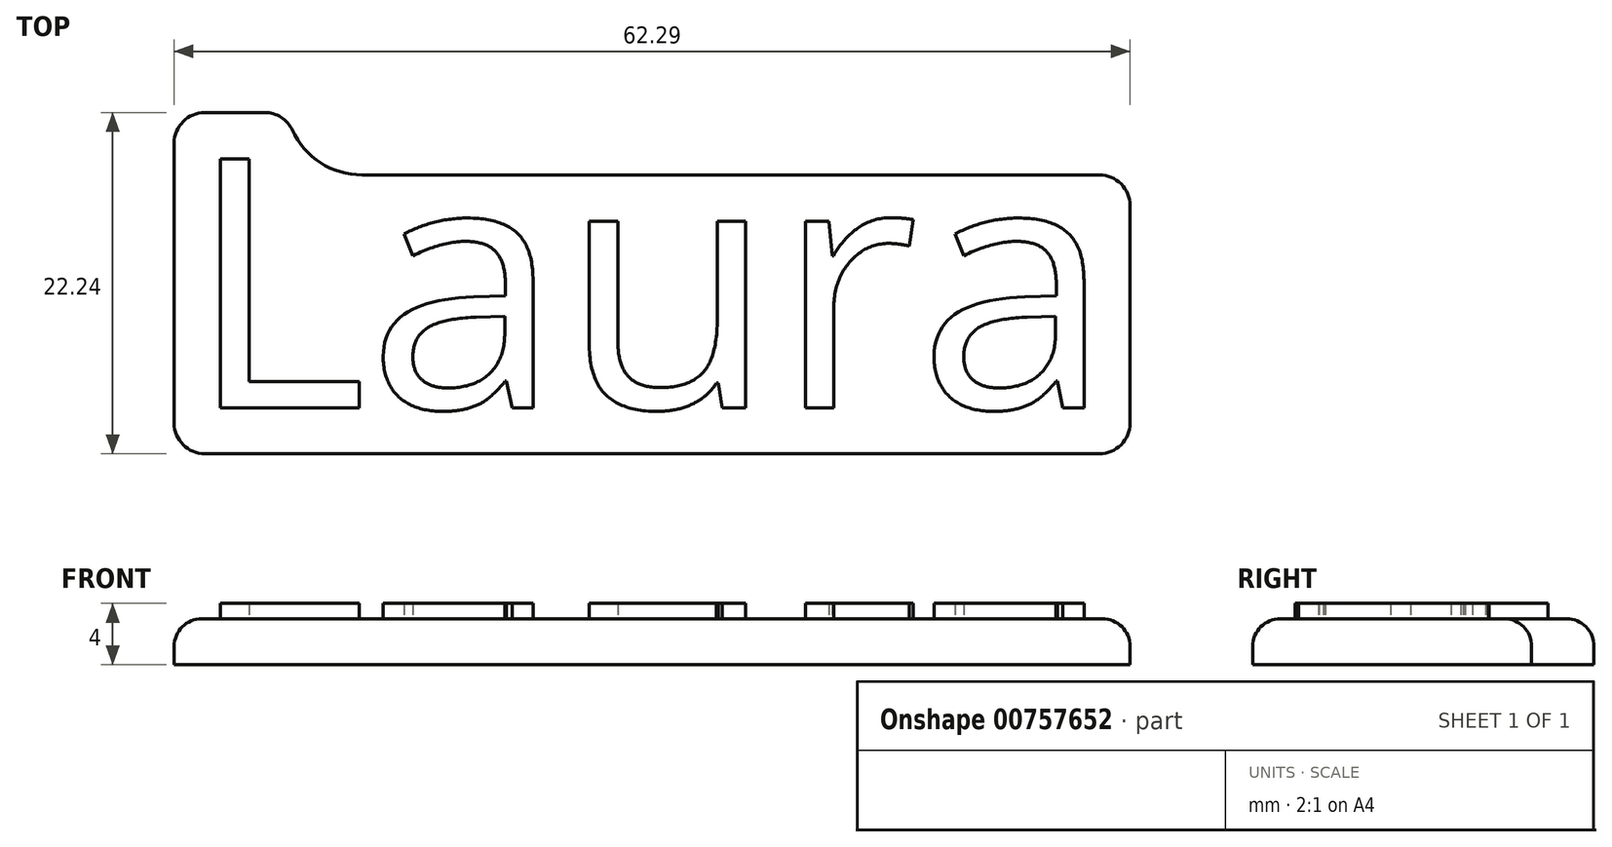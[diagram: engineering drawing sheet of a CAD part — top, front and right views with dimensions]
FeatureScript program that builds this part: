
annotation { "Feature Type Name" : "Feature", "Feature Type Description" : "" }
export const myFeature = defineFeature(function(context is Context, id is Id, definition is map)
    precondition{}
    {
        {
            var Q0;
            Q0=qCreatedBy(makeId("Top.planeOp"),FACE);
            var sketch = newSketch(context, id + "F0", { "sketchPlane" : qUnion([Q0])});
            skText(sketch, "E0", { "text": "Laura", "fontName": "OpenSans-Regular.ttf"});
            skLineSegment(sketch, "E1.bottom", {"start": v(-40, 18.2) * mm, "end": v(40, 18.2) * mm});
            skLineSegment(sketch, "E1.top", {"start": v(-40, -18.2) * mm, "end": v(40, -18.2) * mm});
            skLineSegment(sketch, "E1.left", {"start": v(-40, 18.2) * mm, "end": v(-40, -18.2) * mm});
            skLineSegment(sketch, "E1.right", {"start": v(40, 18.2) * mm, "end": v(40, -18.2) * mm});
            const initialGuessF0  = {"E0": [-0.03, -0.0082, 1, 0, 0.01638]};
            skSetInitialGuess(sketch, initialGuessF0);
            skSolve(sketch);
        }
        {
            var Q0;
            Q0=makeQuery(id+"F0.imprint","IMPRINT",FACE,{"disambiguationData":[TD([[makeQuery(id+"F0.imprint","IMPRINT",EDGE,{"derivedFrom":sQuery(id+"F0.wireOp",EDGE,"E0.sketch_text.stroke-6")}),-1.0]])]});
            var Q1;
            Q1=makeQuery(id+"F0.imprint","IMPRINT",FACE,{"disambiguationData":[TD([[makeQuery(id+"F0.imprint","IMPRINT",EDGE,{"derivedFrom":sQuery(id+"F0.wireOp",EDGE,"E0.sketch_text.stroke-0")}),-1.0]])]});
            var Q2;
            Q2=makeQuery(id+"F0.imprint","IMPRINT",FACE,{"disambiguationData":[TD([[makeQuery(id+"F0.imprint","IMPRINT",EDGE,{"derivedFrom":sQuery(id+"F0.wireOp",EDGE,"E0.sketch_text.stroke-33")}),-1.0]])]});
            var Q3;
            Q3=makeQuery(id+"F0.imprint","IMPRINT",FACE,{"disambiguationData":[TD([[makeQuery(id+"F0.imprint","IMPRINT",EDGE,{"derivedFrom":sQuery(id+"F0.wireOp",EDGE,"E0.sketch_text.stroke-50")}),-1.0]])]});
            var Q4;
            Q4=makeQuery(id+"F0.imprint","IMPRINT",FACE,{"disambiguationData":[TD([[makeQuery(id+"F0.imprint","IMPRINT",EDGE,{"derivedFrom":sQuery(id+"F0.wireOp",EDGE,"E0.sketch_text.stroke-63")}),-1.0]])]});
            extrude(context, id + "F1", {"entities" : qUnion([Q0, Q1, Q2, Q3, Q4]), "depth" : 4 * mm, "offsetDistance" : 25 * mm});
        }
        {
            var Q0;
            Q0=makeQuery(id+"F0.imprint","IMPRINT",FACE,{"disambiguationData":[TD([[makeQuery(id+"F0.imprint","IMPRINT",EDGE,{"derivedFrom":sQuery(id+"F0.wireOp",EDGE,"E0.sketch_text.stroke-0")}),1.0]])]});
            var Q1;
            Q1=makeQuery(id+"F0.imprint","IMPRINT",FACE,{"disambiguationData":[TD([[makeQuery(id+"F0.imprint","IMPRINT",EDGE,{"derivedFrom":sQuery(id+"F0.wireOp",EDGE,"E0.sketch_text.stroke-25")}),1.0]])]});
            var Q2;
            Q2=makeQuery(id+"F0.imprint","IMPRINT",FACE,{"disambiguationData":[TD([[makeQuery(id+"F0.imprint","IMPRINT",EDGE,{"derivedFrom":sQuery(id+"F0.wireOp",EDGE,"E0.sketch_text.stroke-82")}),1.0]])]});
            extrude(context, id + "F2", {"entities" : qUnion([Q0, Q1, Q2]), "operationType" : NewBodyOperationType.ADD, "depth" : 3 * mm, "offsetDistance" : 25 * mm});
        }
        {
            var Q0;
            {var subQ0=sQuery(id+"F0.wireOp",EDGE,"E0.sketch_text.stroke-89");var subQ1=sQuery(id+"F0.wireOp",EDGE,"E0.sketch_text.stroke-88");var subQ2=sQuery(id+"F0.wireOp",EDGE,"E0.sketch_text.stroke-87");var subQ3=sQuery(id+"F0.wireOp",EDGE,"E0.sketch_text.stroke-86");var subQ4=sQuery(id+"F0.wireOp",EDGE,"E0.sketch_text.stroke-85");var subQ5=sQuery(id+"F0.wireOp",EDGE,"E0.sketch_text.stroke-84");var subQ6=sQuery(id+"F0.wireOp",EDGE,"E0.sketch_text.stroke-83");var subQ7=sQuery(id+"F0.wireOp",EDGE,"E0.sketch_text.stroke-82");var subQ8=sQuery(id+"F0.wireOp",EDGE,"E0.sketch_text.stroke-32");var subQ9=sQuery(id+"F0.wireOp",EDGE,"E0.sketch_text.stroke-31");var subQ10=sQuery(id+"F0.wireOp",EDGE,"E0.sketch_text.stroke-30");var subQ11=sQuery(id+"F0.wireOp",EDGE,"E0.sketch_text.stroke-29");var subQ12=sQuery(id+"F0.wireOp",EDGE,"E0.sketch_text.stroke-28");var subQ13=sQuery(id+"F0.wireOp",EDGE,"E0.sketch_text.stroke-27");var subQ14=sQuery(id+"F0.wireOp",EDGE,"E0.sketch_text.stroke-26");var subQ15=sQuery(id+"F0.wireOp",EDGE,"E0.sketch_text.stroke-25");var subQ16=sQuery(id+"F0.wireOp",EDGE,"E0.sketch_text.stroke-81");var subQ17=sQuery(id+"F0.wireOp",EDGE,"E0.sketch_text.stroke-80");var subQ18=sQuery(id+"F0.wireOp",EDGE,"E0.sketch_text.stroke-79");var subQ19=sQuery(id+"F0.wireOp",EDGE,"E0.sketch_text.stroke-78");var subQ20=sQuery(id+"F0.wireOp",EDGE,"E0.sketch_text.stroke-77");var subQ21=sQuery(id+"F0.wireOp",EDGE,"E0.sketch_text.stroke-76");var subQ22=sQuery(id+"F0.wireOp",EDGE,"E0.sketch_text.stroke-75");var subQ23=sQuery(id+"F0.wireOp",EDGE,"E0.sketch_text.stroke-74");var subQ24=sQuery(id+"F0.wireOp",EDGE,"E0.sketch_text.stroke-73");var subQ25=sQuery(id+"F0.wireOp",EDGE,"E0.sketch_text.stroke-72");var subQ26=sQuery(id+"F0.wireOp",EDGE,"E0.sketch_text.stroke-71");var subQ27=sQuery(id+"F0.wireOp",EDGE,"E0.sketch_text.stroke-70");var subQ28=sQuery(id+"F0.wireOp",EDGE,"E0.sketch_text.stroke-69");var subQ29=sQuery(id+"F0.wireOp",EDGE,"E0.sketch_text.stroke-68");var subQ30=sQuery(id+"F0.wireOp",EDGE,"E0.sketch_text.stroke-67");var subQ31=sQuery(id+"F0.wireOp",EDGE,"E0.sketch_text.stroke-66");var subQ32=sQuery(id+"F0.wireOp",EDGE,"E0.sketch_text.stroke-65");var subQ33=sQuery(id+"F0.wireOp",EDGE,"E0.sketch_text.stroke-64");var subQ34=sQuery(id+"F0.wireOp",EDGE,"E0.sketch_text.stroke-63");var subQ35=sQuery(id+"F0.wireOp",EDGE,"E0.sketch_text.stroke-62");var subQ36=sQuery(id+"F0.wireOp",EDGE,"E0.sketch_text.stroke-61");var subQ37=sQuery(id+"F0.wireOp",EDGE,"E0.sketch_text.stroke-60");var subQ38=sQuery(id+"F0.wireOp",EDGE,"E0.sketch_text.stroke-59");var subQ39=sQuery(id+"F0.wireOp",EDGE,"E0.sketch_text.stroke-58");var subQ40=sQuery(id+"F0.wireOp",EDGE,"E0.sketch_text.stroke-57");var subQ41=sQuery(id+"F0.wireOp",EDGE,"E0.sketch_text.stroke-56");var subQ42=sQuery(id+"F0.wireOp",EDGE,"E0.sketch_text.stroke-55");var subQ43=sQuery(id+"F0.wireOp",EDGE,"E0.sketch_text.stroke-54");var subQ44=sQuery(id+"F0.wireOp",EDGE,"E0.sketch_text.stroke-53");var subQ45=sQuery(id+"F0.wireOp",EDGE,"E0.sketch_text.stroke-52");var subQ46=sQuery(id+"F0.wireOp",EDGE,"E0.sketch_text.stroke-51");var subQ47=sQuery(id+"F0.wireOp",EDGE,"E0.sketch_text.stroke-50");var subQ48=sQuery(id+"F0.wireOp",EDGE,"E0.sketch_text.stroke-49");var subQ49=sQuery(id+"F0.wireOp",EDGE,"E0.sketch_text.stroke-48");var subQ50=sQuery(id+"F0.wireOp",EDGE,"E0.sketch_text.stroke-47");var subQ51=sQuery(id+"F0.wireOp",EDGE,"E0.sketch_text.stroke-46");var subQ52=sQuery(id+"F0.wireOp",EDGE,"E0.sketch_text.stroke-45");var subQ53=sQuery(id+"F0.wireOp",EDGE,"E0.sketch_text.stroke-44");var subQ54=sQuery(id+"F0.wireOp",EDGE,"E0.sketch_text.stroke-43");var subQ55=sQuery(id+"F0.wireOp",EDGE,"E0.sketch_text.stroke-42");var subQ56=sQuery(id+"F0.wireOp",EDGE,"E0.sketch_text.stroke-41");var subQ57=sQuery(id+"F0.wireOp",EDGE,"E0.sketch_text.stroke-40");var subQ58=sQuery(id+"F0.wireOp",EDGE,"E0.sketch_text.stroke-39");var subQ59=sQuery(id+"F0.wireOp",EDGE,"E0.sketch_text.stroke-38");var subQ60=sQuery(id+"F0.wireOp",EDGE,"E0.sketch_text.stroke-37");var subQ61=sQuery(id+"F0.wireOp",EDGE,"E0.sketch_text.stroke-36");var subQ62=sQuery(id+"F0.wireOp",EDGE,"E0.sketch_text.stroke-35");var subQ63=sQuery(id+"F0.wireOp",EDGE,"E0.sketch_text.stroke-34");var subQ64=sQuery(id+"F0.wireOp",EDGE,"E0.sketch_text.stroke-33");var subQ65=sQuery(id+"F0.wireOp",EDGE,"E0.sketch_text.stroke-24");var subQ66=sQuery(id+"F0.wireOp",EDGE,"E0.sketch_text.stroke-23");var subQ67=sQuery(id+"F0.wireOp",EDGE,"E0.sketch_text.stroke-22");var subQ68=sQuery(id+"F0.wireOp",EDGE,"E0.sketch_text.stroke-21");var subQ69=sQuery(id+"F0.wireOp",EDGE,"E0.sketch_text.stroke-20");var subQ70=sQuery(id+"F0.wireOp",EDGE,"E0.sketch_text.stroke-19");var subQ71=sQuery(id+"F0.wireOp",EDGE,"E0.sketch_text.stroke-18");var subQ72=sQuery(id+"F0.wireOp",EDGE,"E0.sketch_text.stroke-17");var subQ73=sQuery(id+"F0.wireOp",EDGE,"E0.sketch_text.stroke-16");var subQ74=sQuery(id+"F0.wireOp",EDGE,"E0.sketch_text.stroke-15");var subQ75=sQuery(id+"F0.wireOp",EDGE,"E0.sketch_text.stroke-14");var subQ76=sQuery(id+"F0.wireOp",EDGE,"E0.sketch_text.stroke-13");var subQ77=sQuery(id+"F0.wireOp",EDGE,"E0.sketch_text.stroke-12");var subQ78=sQuery(id+"F0.wireOp",EDGE,"E0.sketch_text.stroke-11");var subQ79=sQuery(id+"F0.wireOp",EDGE,"E0.sketch_text.stroke-10");var subQ80=sQuery(id+"F0.wireOp",EDGE,"E0.sketch_text.stroke-9");var subQ81=sQuery(id+"F0.wireOp",EDGE,"E0.sketch_text.stroke-8");var subQ82=sQuery(id+"F0.wireOp",EDGE,"E0.sketch_text.stroke-7");var subQ83=sQuery(id+"F0.wireOp",EDGE,"E0.sketch_text.stroke-6");var subQ84=sQuery(id+"F0.wireOp",EDGE,"E0.sketch_text.stroke-5");var subQ85=sQuery(id+"F0.wireOp",EDGE,"E0.sketch_text.stroke-4");var subQ86=sQuery(id+"F0.wireOp",EDGE,"E0.sketch_text.stroke-3");var subQ87=sQuery(id+"F0.wireOp",EDGE,"E0.sketch_text.stroke-2");var subQ88=sQuery(id+"F0.wireOp",EDGE,"E0.sketch_text.stroke-1");var subQ89=sQuery(id+"F0.wireOp",EDGE,"E0.sketch_text.stroke-0");Q0=makeQuery(id+"F2.boolean.opBoolean","MERGE",FACE,{"derivedFrom":[makeQuery(id+"F1.opExtrude","CAP_FACE",FACE,{"disambiguationData":[OSD([subQ89,subQ88,subQ87,subQ86,subQ85,subQ84])],"isStart":true}),makeQuery(id+"F1.opExtrude","CAP_FACE",FACE,{"disambiguationData":[OSD([subQ83,subQ82,subQ81,subQ80,subQ79,subQ78,subQ77,subQ76,subQ75,subQ74,subQ73,subQ72,subQ71,subQ70,subQ69,subQ68,subQ67,subQ66,subQ65,subQ15,subQ14,subQ13,subQ12,subQ11,subQ10,subQ9,subQ8])],"isStart":true}),makeQuery(id+"F1.opExtrude","CAP_FACE",FACE,{"disambiguationData":[OSD([subQ64,subQ63,subQ62,subQ61,subQ60,subQ59,subQ58,subQ57,subQ56,subQ55,subQ54,subQ53,subQ52,subQ51,subQ50,subQ49,subQ48])],"isStart":true}),makeQuery(id+"F1.opExtrude","CAP_FACE",FACE,{"disambiguationData":[OSD([subQ47,subQ46,subQ45,subQ44,subQ43,subQ42,subQ41,subQ40,subQ39,subQ38,subQ37,subQ36,subQ35])],"isStart":true}),makeQuery(id+"F1.opExtrude","CAP_FACE",FACE,{"disambiguationData":[OSD([subQ34,subQ33,subQ32,subQ31,subQ30,subQ29,subQ28,subQ27,subQ26,subQ25,subQ24,subQ23,subQ22,subQ21,subQ20,subQ19,subQ18,subQ17,subQ16,subQ7,subQ6,subQ5,subQ4,subQ3,subQ2,subQ1,subQ0])],"isStart":true}),makeQuery(id+"F2.opExtrude","CAP_FACE",FACE,{"disambiguationData":[OSD([subQ89,subQ88,subQ87,subQ86,subQ85,subQ84,subQ83,subQ82,subQ81,subQ80,subQ79,subQ78,subQ77,subQ76,subQ75,subQ74,subQ73,subQ72,subQ71,subQ70,subQ69,subQ68,subQ67,subQ66,subQ65,subQ64,subQ63,subQ62,subQ61,subQ60,subQ59,subQ58,subQ57,subQ56,subQ55,subQ54,subQ53,subQ52,subQ51,subQ50,subQ49,subQ48,subQ47,subQ46,subQ45,subQ44,subQ43,subQ42,subQ41,subQ40,subQ39,subQ38,subQ37,subQ36,subQ35,subQ34,subQ33,subQ32,subQ31,subQ30,subQ29,subQ28,subQ27,subQ26,subQ25,subQ24,subQ23,subQ22,subQ21,subQ20,subQ19,subQ18,subQ17,subQ16,sQuery(id+"F0.wireOp",EDGE,"E1.bottom"),sQuery(id+"F0.wireOp",EDGE,"E1.top"),sQuery(id+"F0.wireOp",EDGE,"E1.left"),sQuery(id+"F0.wireOp",EDGE,"E1.right")])],"isStart":true}),makeQuery(id+"F2.opExtrude","CAP_FACE",FACE,{"disambiguationData":[OSD([subQ15,subQ14,subQ13,subQ12,subQ11,subQ10,subQ9,subQ8])],"isStart":true}),makeQuery(id+"F2.opExtrude","CAP_FACE",FACE,{"disambiguationData":[OSD([subQ7,subQ6,subQ5,subQ4,subQ3,subQ2,subQ1,subQ0])],"isStart":true})]});}
            var sketch = newSketch(context, id + "F3", { "sketchPlane" : qUnion([Q0])});
            skLineSegment(sketch, "E2.0.0", {"start": v(-40, -18.2) * mm, "end": v(-40, 18.2) * mm});
            skLineSegment(sketch, "E2.0.1", {"start": v(-40, 18.2) * mm, "end": v(40, 18.2) * mm});
            skLineSegment(sketch, "E2.0.2", {"start": v(40, 18.2) * mm, "end": v(40, -18.2) * mm});
            skLineSegment(sketch, "E2.0.3", {"start": v(40, -18.2) * mm, "end": v(-40, -18.2) * mm});
            skLineSegment(sketch, "E3.0.0", {"start": v(-27.77, 8.2) * mm, "end": v(-18.71, 8.2) * mm});
            skLineSegment(sketch, "E3.0.1", {"start": v(-18.71, 8.2) * mm, "end": v(-18.71, 6.48) * mm});
            skLineSegment(sketch, "E3.0.2", {"start": v(-18.71, 6.48) * mm, "end": v(-25.88, 6.48) * mm});
            skLineSegment(sketch, "E3.0.3", {"start": v(-25.88, 6.48) * mm, "end": v(-25.88, -8.05) * mm});
            skLineSegment(sketch, "E3.0.4", {"start": v(-25.88, -8.05) * mm, "end": v(-27.77, -8.05) * mm});
            skLineSegment(sketch, "E3.0.5", {"start": v(-27.77, -8.05) * mm, "end": v(-27.77, 8.2) * mm});
            skLineSegment(sketch, "E3.1.0", {"start": v(-8.75, 8.2) * mm, "end": v(-7.38, 8.2) * mm});
            skLineSegment(sketch, "E3.1.1", {"start": v(-7.38, 8.2) * mm, "end": v(-7.38, -0.12) * mm});
            skFitSpline(sketch, "E3.1.2", {"points": [v(-3.7, -0.06) * mm, v(-3.7, -1.13) * mm, v(-4.22, -1.6) * mm]});
            skFitSpline(sketch, "E3.1.3", {"points": [v(-4.22, -1.6) * mm, v(-4.74, -2.1) * mm, v(-5.83, -2.1) * mm]});
            skFitSpline(sketch, "E3.1.4", {"points": [v(-5.83, -2.1) * mm, v(-6.37, -2.1) * mm, v(-6.9, -1.95) * mm]});
            skFitSpline(sketch, "E3.1.5", {"points": [v(-6.9, -1.95) * mm, v(-7.44, -1.81) * mm, v(-7.9, -1.57) * mm]});
            skLineSegment(sketch, "E3.1.6", {"start": v(-15.78, -3.14) * mm, "end": v(-15.21, -1.73) * mm});
            skFitSpline(sketch, "E3.1.7", {"points": [v(-7.6, -0.87) * mm, v(-6.65, -1.33) * mm, v(-5.89, -1.33) * mm]});
            skFitSpline(sketch, "E3.1.8", {"points": [v(-5.89, -1.33) * mm, v(-5.2, -1.33) * mm, v(-4.9, -1) * mm]});
            skFitSpline(sketch, "E3.1.9", {"points": [v(-4.9, -1) * mm, v(-4.6, -0.65) * mm, v(-4.6, 0.07) * mm]});
            skLineSegment(sketch, "E3.1.10", {"start": v(-9.18, 0.14) * mm, "end": v(-9.18, 0.9) * mm});
            skLineSegment(sketch, "E3.1.11", {"start": v(-9.18, 0.9) * mm, "end": v(-11.25, 0.96) * mm});
            skFitSpline(sketch, "E3.1.12", {"points": [v(-5.62, 0.48) * mm, v(-8.57, 0.57) * mm, v(-8.57, 2.41) * mm]});
            skFitSpline(sketch, "E3.1.13", {"points": [v(-8.57, 2.41) * mm, v(-8.57, 3.27) * mm, v(-8.06, 3.74) * mm]});
            skFitSpline(sketch, "E3.1.14", {"points": [v(-8.06, 3.74) * mm, v(-7.55, 4.2) * mm, v(-6.64, 4.2) * mm]});
            skFitSpline(sketch, "E3.1.15", {"points": [v(-6.64, 4.2) * mm, v(-5.96, 4.2) * mm, v(-5.5, 4) * mm]});
            skFitSpline(sketch, "E3.1.16", {"points": [v(-5.5, 4) * mm, v(-5.06, 3.8) * mm, v(-4.6, 3.23) * mm]});
            skLineSegment(sketch, "E3.1.17", {"start": v(-9.2, 6.46) * mm, "end": v(-9.11, 6.46) * mm});
            skLineSegment(sketch, "E3.1.18", {"start": v(-9.11, 6.46) * mm, "end": v(-8.75, 8.2) * mm});
            skLineSegment(sketch, "E3.2.0", {"start": v(-1.85, -3.99) * mm, "end": v(-3.71, -3.99) * mm});
            skLineSegment(sketch, "E3.2.1", {"start": v(-3.71, -3.99) * mm, "end": v(-3.71, 3.98) * mm});
            skFitSpline(sketch, "E3.2.2", {"points": [v(-1.86, 2) * mm, v(-1.86, 3.15) * mm, v(-1.3, 3.68) * mm]});
            skFitSpline(sketch, "E3.2.3", {"points": [v(-1.3, 3.68) * mm, v(-0.75, 4.2) * mm, v(0.36, 4.2) * mm]});
            skFitSpline(sketch, "E3.2.4", {"points": [v(0.36, 4.2) * mm, v(1, 4.2) * mm, v(1.5, 3.97) * mm]});
            skFitSpline(sketch, "E3.2.5", {"points": [v(1.5, 3.97) * mm, v(2, 3.73) * mm, v(2.3, 3.28) * mm]});
            skLineSegment(sketch, "E3.2.6", {"start": v(4.58, 6.56) * mm, "end": v(4.68, 6.56) * mm});
            skLineSegment(sketch, "E3.2.7", {"start": v(4.68, 6.56) * mm, "end": v(4.95, 8.2) * mm});
            skLineSegment(sketch, "E3.2.8", {"start": v(4.95, 8.2) * mm, "end": v(6.47, 8.2) * mm});
            skLineSegment(sketch, "E3.2.9", {"start": v(6.47, 8.2) * mm, "end": v(6.47, -3.99) * mm});
            skLineSegment(sketch, "E3.2.10", {"start": v(6.47, -3.99) * mm, "end": v(4.62, -3.99) * mm});
            skLineSegment(sketch, "E3.2.11", {"start": v(4.62, -3.99) * mm, "end": v(4.62, 2.41) * mm});
            skFitSpline(sketch, "E3.2.12", {"points": [v(2.31, 1.2) * mm, v(2.31, 2.4) * mm, v(1.87, 2.91) * mm]});
            skFitSpline(sketch, "E3.2.13", {"points": [v(1.87, 2.91) * mm, v(1.43, 3.43) * mm, v(0.47, 3.43) * mm]});
            skFitSpline(sketch, "E3.2.14", {"points": [v(0.47, 3.43) * mm, v(-0.25, 3.43) * mm, v(-0.59, 3.07) * mm]});
            skFitSpline(sketch, "E3.2.15", {"points": [v(-0.59, 3.07) * mm, v(-0.92, 2.7) * mm, v(-0.92, 1.96) * mm]});
            skLineSegment(sketch, "E3.2.16", {"start": v(-1.85, 3.91) * mm, "end": v(-1.85, -3.99) * mm});
            skFitSpline(sketch, "E3.3.0", {"points": [v(7.97, -2.1) * mm, v(7.4, -2.1) * mm, v(6.92, -1.78) * mm]});
            skFitSpline(sketch, "E3.3.1", {"points": [v(6.92, -1.78) * mm, v(6.44, -1.46) * mm, v(6.1, -0.87) * mm]});
            skLineSegment(sketch, "E3.3.2", {"start": v(12.2, -1.73) * mm, "end": v(12.12, -1.73) * mm});
            skLineSegment(sketch, "E3.3.3", {"start": v(12.12, -1.73) * mm, "end": v(11.9, -3.99) * mm});
            skLineSegment(sketch, "E3.3.4", {"start": v(11.9, -3.99) * mm, "end": v(10.38, -3.99) * mm});
            skLineSegment(sketch, "E3.3.5", {"start": v(10.38, -3.99) * mm, "end": v(10.38, 8.2) * mm});
            skLineSegment(sketch, "E3.3.6", {"start": v(10.38, 8.2) * mm, "end": v(12.23, 8.2) * mm});
            skLineSegment(sketch, "E3.3.7", {"start": v(12.23, 8.2) * mm, "end": v(12.23, 1.66) * mm});
            skFitSpline(sketch, "E3.3.8", {"points": [v(6.11, 0.83) * mm, v(6.11, -0.07) * mm, v(6.64, -0.67) * mm]});
            skFitSpline(sketch, "E3.3.9", {"points": [v(6.64, -0.67) * mm, v(7.16, -1.27) * mm, v(7.9, -1.27) * mm]});
            skFitSpline(sketch, "E3.3.10", {"points": [v(7.9, -1.27) * mm, v(8.2, -1.27) * mm, v(8.57, -1.18) * mm]});
            skLineSegment(sketch, "E3.3.11", {"start": v(17.13, -2.36) * mm, "end": v(17.4, -4.07) * mm});
            skFitSpline(sketch, "E3.3.12", {"points": [v(8.7, -2.04) * mm, v(8.37, -2.1) * mm, v(7.97, -2.1) * mm]});
            skLineSegment(sketch, "E3.4.0", {"start": v(27.16, 8.2) * mm, "end": v(28.52, 8.2) * mm});
            skLineSegment(sketch, "E3.4.1", {"start": v(28.52, 8.2) * mm, "end": v(28.52, -0.12) * mm});
            skFitSpline(sketch, "E3.4.2", {"points": [v(14.26, -0.06) * mm, v(14.26, -1.13) * mm, v(13.74, -1.6) * mm]});
            skFitSpline(sketch, "E3.4.3", {"points": [v(13.74, -1.6) * mm, v(13.21, -2.1) * mm, v(12.12, -2.1) * mm]});
            skFitSpline(sketch, "E3.4.4", {"points": [v(12.12, -2.1) * mm, v(11.58, -2.1) * mm, v(11.05, -1.95) * mm]});
            skFitSpline(sketch, "E3.4.5", {"points": [v(11.05, -1.95) * mm, v(10.51, -1.81) * mm, v(10.06, -1.57) * mm]});
            skLineSegment(sketch, "E3.4.6", {"start": v(20.12, -3.14) * mm, "end": v(20.7, -1.73) * mm});
            skFitSpline(sketch, "E3.4.7", {"points": [v(10.35, -0.87) * mm, v(11.3, -1.33) * mm, v(12.07, -1.33) * mm]});
            skFitSpline(sketch, "E3.4.8", {"points": [v(12.07, -1.33) * mm, v(12.75, -1.33) * mm, v(13.05, -1) * mm]});
            skFitSpline(sketch, "E3.4.9", {"points": [v(13.05, -1) * mm, v(13.36, -0.65) * mm, v(13.36, 0.07) * mm]});
            skLineSegment(sketch, "E3.4.10", {"start": v(26.72, 0.14) * mm, "end": v(26.72, 0.9) * mm});
            skLineSegment(sketch, "E3.4.11", {"start": v(26.72, 0.9) * mm, "end": v(24.66, 0.96) * mm});
            skFitSpline(sketch, "E3.4.12", {"points": [v(12.33, 0.48) * mm, v(9.38, 0.57) * mm, v(9.38, 2.41) * mm]});
            skFitSpline(sketch, "E3.4.13", {"points": [v(9.38, 2.41) * mm, v(9.38, 3.27) * mm, v(9.9, 3.74) * mm]});
            skFitSpline(sketch, "E3.4.14", {"points": [v(9.9, 3.74) * mm, v(10.4, 4.2) * mm, v(11.31, 4.2) * mm]});
            skFitSpline(sketch, "E3.4.15", {"points": [v(11.31, 4.2) * mm, v(12, 4.2) * mm, v(12.44, 4) * mm]});
            skFitSpline(sketch, "E3.4.16", {"points": [v(12.44, 4) * mm, v(12.9, 3.8) * mm, v(13.35, 3.23) * mm]});
            skLineSegment(sketch, "E3.4.17", {"start": v(26.7, 6.46) * mm, "end": v(26.79, 6.46) * mm});
            skLineSegment(sketch, "E3.4.18", {"start": v(26.79, 6.46) * mm, "end": v(27.16, 8.2) * mm});
            skFitSpline(sketch, "E4.0.0", {"points": [v(-7.6, 2.42) * mm, v(-7.6, 2.92) * mm, v(-7.3, 3.18) * mm]});
            skFitSpline(sketch, "E4.0.1", {"points": [v(-7.3, 3.18) * mm, v(-7, 3.44) * mm, v(-6.46, 3.44) * mm]});
            skFitSpline(sketch, "E4.0.2", {"points": [v(-6.46, 3.44) * mm, v(-5.6, 3.44) * mm, v(-5.1, 2.97) * mm]});
            skFitSpline(sketch, "E4.0.3", {"points": [v(-5.1, 2.97) * mm, v(-4.61, 2.5) * mm, v(-4.61, 1.65) * mm]});
            skLineSegment(sketch, "E4.0.4", {"start": v(-9.23, 3.3) * mm, "end": v(-9.23, 2.2) * mm});
            skLineSegment(sketch, "E4.0.5", {"start": v(-9.23, 2.2) * mm, "end": v(-11.07, 2.28) * mm});
            skFitSpline(sketch, "E4.0.6", {"points": [v(-5.54, 1.14) * mm, v(-6.64, 1.18) * mm, v(-7.12, 1.48) * mm]});
            skFitSpline(sketch, "E4.0.7", {"points": [v(-7.12, 1.48) * mm, v(-7.6, 1.78) * mm, v(-7.6, 2.42) * mm]});
            skFitSpline(sketch, "E4.1.0", {"points": [v(10.35, 2.42) * mm, v(10.35, 2.92) * mm, v(10.65, 3.18) * mm]});
            skFitSpline(sketch, "E4.1.1", {"points": [v(10.65, 3.18) * mm, v(10.95, 3.44) * mm, v(11.5, 3.44) * mm]});
            skFitSpline(sketch, "E4.1.2", {"points": [v(11.5, 3.44) * mm, v(12.36, 3.44) * mm, v(12.85, 2.97) * mm]});
            skFitSpline(sketch, "E4.1.3", {"points": [v(12.85, 2.97) * mm, v(13.34, 2.5) * mm, v(13.34, 1.65) * mm]});
            skLineSegment(sketch, "E4.1.4", {"start": v(26.68, 3.3) * mm, "end": v(26.68, 2.2) * mm});
            skLineSegment(sketch, "E4.1.5", {"start": v(26.68, 2.2) * mm, "end": v(24.83, 2.28) * mm});
            skFitSpline(sketch, "E4.1.6", {"points": [v(12.42, 1.14) * mm, v(11.32, 1.18) * mm, v(10.83, 1.48) * mm]});
            skFitSpline(sketch, "E4.1.7", {"points": [v(10.83, 1.48) * mm, v(10.35, 1.78) * mm, v(10.35, 2.42) * mm]});
            skLineSegment(sketch, "E5.0", {"start": v(-30.77, 11.2) * mm, "end": v(31.52, 11.2) * mm});
            skLineSegment(sketch, "E5.1", {"start": v(-30.77, -11.05) * mm, "end": v(-30.77, 11.2) * mm});
            skLineSegment(sketch, "E5.2", {"start": v(-22.88, -11.05) * mm, "end": v(-30.77, -11.05) * mm});
            skLineSegment(sketch, "E6", {"start": v(31.52, -6.99) * mm, "end": v(31.52, 11.2) * mm});
            skLineSegment(sketch, "E7", {"start": v(31.52, -6.99) * mm, "end": v(-22.88, -6.99) * mm});
            skLineSegment(sketch, "E8", {"start": v(-22.88, -6.99) * mm, "end": v(-22.88, -11.05) * mm});
            skSolve(sketch);
        }
        {
            var Q0;
            Q0=makeQuery(id+"F3.imprint","IMPRINT",FACE,{"disambiguationData":[TD([[makeQuery(id+"F3.imprint","IMPRINT",EDGE,{"derivedFrom":sQuery(id+"F3.wireOp",EDGE,"E2.0.0")}),-1.0]])]});
            extrude(context, id + "F4", {"entities" : qUnion([Q0]), "operationType" : NewBodyOperationType.REMOVE, "oppositeDirection" : true, "depth" : 25 * mm, "offsetDistance" : 25 * mm});
        }
        {
            var Q0;
            Q0=makeQuery(id+"F4.boolean.opBoolean","COPY",EDGE,{"derivedFrom":makeQuery(id+"F4.opExtrude","SWEPT_EDGE",EDGE,{"disambiguationData":[OSD([sQuery(id+"F3.wireOp",EDGE,"E5.2"),sQuery(id+"F3.wireOp",EDGE,"E8")])]})});
            var Q1;
            Q1=makeQuery(id+"F4.boolean.opBoolean","COPY",EDGE,{"derivedFrom":makeQuery(id+"F4.opExtrude","SWEPT_EDGE",EDGE,{"disambiguationData":[OSD([sQuery(id+"F3.wireOp",EDGE,"E5.1"),sQuery(id+"F3.wireOp",EDGE,"E5.2")])]})});
            var Q2;
            Q2=makeQuery(id+"F4.boolean.opBoolean","COPY",EDGE,{"derivedFrom":makeQuery(id+"F4.opExtrude","SWEPT_EDGE",EDGE,{"disambiguationData":[OSD([sQuery(id+"F3.wireOp",EDGE,"E5.0"),sQuery(id+"F3.wireOp",EDGE,"E5.1")])]})});
            var Q3;
            Q3=makeQuery(id+"F4.boolean.opBoolean","COPY",EDGE,{"derivedFrom":makeQuery(id+"F4.opExtrude","SWEPT_EDGE",EDGE,{"disambiguationData":[OSD([sQuery(id+"F3.wireOp",EDGE,"E5.0"),sQuery(id+"F3.wireOp",EDGE,"E6")])]})});
            var Q4;
            Q4=makeQuery(id+"F4.boolean.opBoolean","COPY",EDGE,{"derivedFrom":makeQuery(id+"F4.opExtrude","SWEPT_EDGE",EDGE,{"disambiguationData":[OSD([sQuery(id+"F3.wireOp",EDGE,"E6"),sQuery(id+"F3.wireOp",EDGE,"E7")])]})});
            fillet(context, id + "F5", {"entities" : qUnion([Q0, Q1, Q2, Q3, Q4]), "tangentPropagation" : true, "radius" : 2 * mm, "defaultsChanged" : true, "vertexSettings" : [], "allowEdgeOverflow" : false});
        }
        {
            var Q0;
            Q0=makeQuery(id+"F4.boolean.opBoolean","COPY",EDGE,{"derivedFrom":makeQuery(id+"F4.opExtrude","SWEPT_EDGE",EDGE,{"disambiguationData":[OSD([sQuery(id+"F3.wireOp",EDGE,"E7"),sQuery(id+"F3.wireOp",EDGE,"E8")])]})});
            fillet(context, id + "F6", {"entities" : qUnion([Q0]), "tangentPropagation" : true, "radius" : 5 * mm, "defaultsChanged" : false, "vertexSettings" : [], "allowEdgeOverflow" : false});
        }
        {
            var Q0;
            Q0=makeQuery(id+"F4.boolean.opBoolean","INTERSECT",EDGE,{"derivedFrom":[makeQuery(id+"F2.opExtrude","CAP_FACE",FACE,{"disambiguationData":[OSD([sQuery(id+"F0.wireOp",EDGE,"E0.sketch_text.stroke-0"),sQuery(id+"F0.wireOp",EDGE,"E0.sketch_text.stroke-1"),sQuery(id+"F0.wireOp",EDGE,"E0.sketch_text.stroke-2"),sQuery(id+"F0.wireOp",EDGE,"E0.sketch_text.stroke-3"),sQuery(id+"F0.wireOp",EDGE,"E0.sketch_text.stroke-4"),sQuery(id+"F0.wireOp",EDGE,"E0.sketch_text.stroke-5"),sQuery(id+"F0.wireOp",EDGE,"E0.sketch_text.stroke-6"),sQuery(id+"F0.wireOp",EDGE,"E0.sketch_text.stroke-7"),sQuery(id+"F0.wireOp",EDGE,"E0.sketch_text.stroke-8"),sQuery(id+"F0.wireOp",EDGE,"E0.sketch_text.stroke-9"),sQuery(id+"F0.wireOp",EDGE,"E0.sketch_text.stroke-10"),sQuery(id+"F0.wireOp",EDGE,"E0.sketch_text.stroke-11"),sQuery(id+"F0.wireOp",EDGE,"E0.sketch_text.stroke-12"),sQuery(id+"F0.wireOp",EDGE,"E0.sketch_text.stroke-13"),sQuery(id+"F0.wireOp",EDGE,"E0.sketch_text.stroke-14"),sQuery(id+"F0.wireOp",EDGE,"E0.sketch_text.stroke-15"),sQuery(id+"F0.wireOp",EDGE,"E0.sketch_text.stroke-16"),sQuery(id+"F0.wireOp",EDGE,"E0.sketch_text.stroke-17"),sQuery(id+"F0.wireOp",EDGE,"E0.sketch_text.stroke-18"),sQuery(id+"F0.wireOp",EDGE,"E0.sketch_text.stroke-19"),sQuery(id+"F0.wireOp",EDGE,"E0.sketch_text.stroke-20"),sQuery(id+"F0.wireOp",EDGE,"E0.sketch_text.stroke-21"),sQuery(id+"F0.wireOp",EDGE,"E0.sketch_text.stroke-22"),sQuery(id+"F0.wireOp",EDGE,"E0.sketch_text.stroke-23"),sQuery(id+"F0.wireOp",EDGE,"E0.sketch_text.stroke-24"),sQuery(id+"F0.wireOp",EDGE,"E0.sketch_text.stroke-33"),sQuery(id+"F0.wireOp",EDGE,"E0.sketch_text.stroke-34"),sQuery(id+"F0.wireOp",EDGE,"E0.sketch_text.stroke-35"),sQuery(id+"F0.wireOp",EDGE,"E0.sketch_text.stroke-36"),sQuery(id+"F0.wireOp",EDGE,"E0.sketch_text.stroke-37"),sQuery(id+"F0.wireOp",EDGE,"E0.sketch_text.stroke-38"),sQuery(id+"F0.wireOp",EDGE,"E0.sketch_text.stroke-39"),sQuery(id+"F0.wireOp",EDGE,"E0.sketch_text.stroke-40"),sQuery(id+"F0.wireOp",EDGE,"E0.sketch_text.stroke-41"),sQuery(id+"F0.wireOp",EDGE,"E0.sketch_text.stroke-42"),sQuery(id+"F0.wireOp",EDGE,"E0.sketch_text.stroke-43"),sQuery(id+"F0.wireOp",EDGE,"E0.sketch_text.stroke-44"),sQuery(id+"F0.wireOp",EDGE,"E0.sketch_text.stroke-45"),sQuery(id+"F0.wireOp",EDGE,"E0.sketch_text.stroke-46"),sQuery(id+"F0.wireOp",EDGE,"E0.sketch_text.stroke-47"),sQuery(id+"F0.wireOp",EDGE,"E0.sketch_text.stroke-48"),sQuery(id+"F0.wireOp",EDGE,"E0.sketch_text.stroke-49"),sQuery(id+"F0.wireOp",EDGE,"E0.sketch_text.stroke-50"),sQuery(id+"F0.wireOp",EDGE,"E0.sketch_text.stroke-51"),sQuery(id+"F0.wireOp",EDGE,"E0.sketch_text.stroke-52"),sQuery(id+"F0.wireOp",EDGE,"E0.sketch_text.stroke-53"),sQuery(id+"F0.wireOp",EDGE,"E0.sketch_text.stroke-54"),sQuery(id+"F0.wireOp",EDGE,"E0.sketch_text.stroke-55"),sQuery(id+"F0.wireOp",EDGE,"E0.sketch_text.stroke-56"),sQuery(id+"F0.wireOp",EDGE,"E0.sketch_text.stroke-57"),sQuery(id+"F0.wireOp",EDGE,"E0.sketch_text.stroke-58"),sQuery(id+"F0.wireOp",EDGE,"E0.sketch_text.stroke-59"),sQuery(id+"F0.wireOp",EDGE,"E0.sketch_text.stroke-60"),sQuery(id+"F0.wireOp",EDGE,"E0.sketch_text.stroke-61"),sQuery(id+"F0.wireOp",EDGE,"E0.sketch_text.stroke-62"),sQuery(id+"F0.wireOp",EDGE,"E0.sketch_text.stroke-63"),sQuery(id+"F0.wireOp",EDGE,"E0.sketch_text.stroke-64"),sQuery(id+"F0.wireOp",EDGE,"E0.sketch_text.stroke-65"),sQuery(id+"F0.wireOp",EDGE,"E0.sketch_text.stroke-66"),sQuery(id+"F0.wireOp",EDGE,"E0.sketch_text.stroke-67"),sQuery(id+"F0.wireOp",EDGE,"E0.sketch_text.stroke-68"),sQuery(id+"F0.wireOp",EDGE,"E0.sketch_text.stroke-69"),sQuery(id+"F0.wireOp",EDGE,"E0.sketch_text.stroke-70"),sQuery(id+"F0.wireOp",EDGE,"E0.sketch_text.stroke-71"),sQuery(id+"F0.wireOp",EDGE,"E0.sketch_text.stroke-72"),sQuery(id+"F0.wireOp",EDGE,"E0.sketch_text.stroke-73"),sQuery(id+"F0.wireOp",EDGE,"E0.sketch_text.stroke-74"),sQuery(id+"F0.wireOp",EDGE,"E0.sketch_text.stroke-75"),sQuery(id+"F0.wireOp",EDGE,"E0.sketch_text.stroke-76"),sQuery(id+"F0.wireOp",EDGE,"E0.sketch_text.stroke-77"),sQuery(id+"F0.wireOp",EDGE,"E0.sketch_text.stroke-78"),sQuery(id+"F0.wireOp",EDGE,"E0.sketch_text.stroke-79"),sQuery(id+"F0.wireOp",EDGE,"E0.sketch_text.stroke-80"),sQuery(id+"F0.wireOp",EDGE,"E0.sketch_text.stroke-81"),sQuery(id+"F0.wireOp",EDGE,"E1.bottom"),sQuery(id+"F0.wireOp",EDGE,"E1.top"),sQuery(id+"F0.wireOp",EDGE,"E1.left"),sQuery(id+"F0.wireOp",EDGE,"E1.right")])],"isStart":false}),makeQuery(id+"F4.opExtrude","SWEPT_FACE",FACE,{"disambiguationData":[OSD([sQuery(id+"F3.wireOp",EDGE,"E5.0")])]})]});
            var Q1;
            Q1=makeQuery(id+"F5.opFillet","BLEND_EDGE",EDGE,{"blendedFrom":[makeQuery(id+"F4.boolean.opBoolean","COPY",EDGE,{"derivedFrom":makeQuery(id+"F4.opExtrude","SWEPT_EDGE",EDGE,{"disambiguationData":[OSD([sQuery(id+"F3.wireOp",EDGE,"E5.0"),sQuery(id+"F3.wireOp",EDGE,"E5.1")])]})}),makeQuery(id+"F2.opExtrude","CAP_FACE",FACE,{"disambiguationData":[OSD([sQuery(id+"F0.wireOp",EDGE,"E0.sketch_text.stroke-0"),sQuery(id+"F0.wireOp",EDGE,"E0.sketch_text.stroke-1"),sQuery(id+"F0.wireOp",EDGE,"E0.sketch_text.stroke-2"),sQuery(id+"F0.wireOp",EDGE,"E0.sketch_text.stroke-3"),sQuery(id+"F0.wireOp",EDGE,"E0.sketch_text.stroke-4"),sQuery(id+"F0.wireOp",EDGE,"E0.sketch_text.stroke-5"),sQuery(id+"F0.wireOp",EDGE,"E0.sketch_text.stroke-6"),sQuery(id+"F0.wireOp",EDGE,"E0.sketch_text.stroke-7"),sQuery(id+"F0.wireOp",EDGE,"E0.sketch_text.stroke-8"),sQuery(id+"F0.wireOp",EDGE,"E0.sketch_text.stroke-9"),sQuery(id+"F0.wireOp",EDGE,"E0.sketch_text.stroke-10"),sQuery(id+"F0.wireOp",EDGE,"E0.sketch_text.stroke-11"),sQuery(id+"F0.wireOp",EDGE,"E0.sketch_text.stroke-12"),sQuery(id+"F0.wireOp",EDGE,"E0.sketch_text.stroke-13"),sQuery(id+"F0.wireOp",EDGE,"E0.sketch_text.stroke-14"),sQuery(id+"F0.wireOp",EDGE,"E0.sketch_text.stroke-15"),sQuery(id+"F0.wireOp",EDGE,"E0.sketch_text.stroke-16"),sQuery(id+"F0.wireOp",EDGE,"E0.sketch_text.stroke-17"),sQuery(id+"F0.wireOp",EDGE,"E0.sketch_text.stroke-18"),sQuery(id+"F0.wireOp",EDGE,"E0.sketch_text.stroke-19"),sQuery(id+"F0.wireOp",EDGE,"E0.sketch_text.stroke-20"),sQuery(id+"F0.wireOp",EDGE,"E0.sketch_text.stroke-21"),sQuery(id+"F0.wireOp",EDGE,"E0.sketch_text.stroke-22"),sQuery(id+"F0.wireOp",EDGE,"E0.sketch_text.stroke-23"),sQuery(id+"F0.wireOp",EDGE,"E0.sketch_text.stroke-24"),sQuery(id+"F0.wireOp",EDGE,"E0.sketch_text.stroke-33"),sQuery(id+"F0.wireOp",EDGE,"E0.sketch_text.stroke-34"),sQuery(id+"F0.wireOp",EDGE,"E0.sketch_text.stroke-35"),sQuery(id+"F0.wireOp",EDGE,"E0.sketch_text.stroke-36"),sQuery(id+"F0.wireOp",EDGE,"E0.sketch_text.stroke-37"),sQuery(id+"F0.wireOp",EDGE,"E0.sketch_text.stroke-38"),sQuery(id+"F0.wireOp",EDGE,"E0.sketch_text.stroke-39"),sQuery(id+"F0.wireOp",EDGE,"E0.sketch_text.stroke-40"),sQuery(id+"F0.wireOp",EDGE,"E0.sketch_text.stroke-41"),sQuery(id+"F0.wireOp",EDGE,"E0.sketch_text.stroke-42"),sQuery(id+"F0.wireOp",EDGE,"E0.sketch_text.stroke-43"),sQuery(id+"F0.wireOp",EDGE,"E0.sketch_text.stroke-44"),sQuery(id+"F0.wireOp",EDGE,"E0.sketch_text.stroke-45"),sQuery(id+"F0.wireOp",EDGE,"E0.sketch_text.stroke-46"),sQuery(id+"F0.wireOp",EDGE,"E0.sketch_text.stroke-47"),sQuery(id+"F0.wireOp",EDGE,"E0.sketch_text.stroke-48"),sQuery(id+"F0.wireOp",EDGE,"E0.sketch_text.stroke-49"),sQuery(id+"F0.wireOp",EDGE,"E0.sketch_text.stroke-50"),sQuery(id+"F0.wireOp",EDGE,"E0.sketch_text.stroke-51"),sQuery(id+"F0.wireOp",EDGE,"E0.sketch_text.stroke-52"),sQuery(id+"F0.wireOp",EDGE,"E0.sketch_text.stroke-53"),sQuery(id+"F0.wireOp",EDGE,"E0.sketch_text.stroke-54"),sQuery(id+"F0.wireOp",EDGE,"E0.sketch_text.stroke-55"),sQuery(id+"F0.wireOp",EDGE,"E0.sketch_text.stroke-56"),sQuery(id+"F0.wireOp",EDGE,"E0.sketch_text.stroke-57"),sQuery(id+"F0.wireOp",EDGE,"E0.sketch_text.stroke-58"),sQuery(id+"F0.wireOp",EDGE,"E0.sketch_text.stroke-59"),sQuery(id+"F0.wireOp",EDGE,"E0.sketch_text.stroke-60"),sQuery(id+"F0.wireOp",EDGE,"E0.sketch_text.stroke-61"),sQuery(id+"F0.wireOp",EDGE,"E0.sketch_text.stroke-62"),sQuery(id+"F0.wireOp",EDGE,"E0.sketch_text.stroke-63"),sQuery(id+"F0.wireOp",EDGE,"E0.sketch_text.stroke-64"),sQuery(id+"F0.wireOp",EDGE,"E0.sketch_text.stroke-65"),sQuery(id+"F0.wireOp",EDGE,"E0.sketch_text.stroke-66"),sQuery(id+"F0.wireOp",EDGE,"E0.sketch_text.stroke-67"),sQuery(id+"F0.wireOp",EDGE,"E0.sketch_text.stroke-68"),sQuery(id+"F0.wireOp",EDGE,"E0.sketch_text.stroke-69"),sQuery(id+"F0.wireOp",EDGE,"E0.sketch_text.stroke-70"),sQuery(id+"F0.wireOp",EDGE,"E0.sketch_text.stroke-71"),sQuery(id+"F0.wireOp",EDGE,"E0.sketch_text.stroke-72"),sQuery(id+"F0.wireOp",EDGE,"E0.sketch_text.stroke-73"),sQuery(id+"F0.wireOp",EDGE,"E0.sketch_text.stroke-74"),sQuery(id+"F0.wireOp",EDGE,"E0.sketch_text.stroke-75"),sQuery(id+"F0.wireOp",EDGE,"E0.sketch_text.stroke-76"),sQuery(id+"F0.wireOp",EDGE,"E0.sketch_text.stroke-77"),sQuery(id+"F0.wireOp",EDGE,"E0.sketch_text.stroke-78"),sQuery(id+"F0.wireOp",EDGE,"E0.sketch_text.stroke-79"),sQuery(id+"F0.wireOp",EDGE,"E0.sketch_text.stroke-80"),sQuery(id+"F0.wireOp",EDGE,"E0.sketch_text.stroke-81"),sQuery(id+"F0.wireOp",EDGE,"E1.bottom"),sQuery(id+"F0.wireOp",EDGE,"E1.top"),sQuery(id+"F0.wireOp",EDGE,"E1.left"),sQuery(id+"F0.wireOp",EDGE,"E1.right")])],"isStart":false})],"blendedInto":[makeQuery(id+"F2.opExtrude","CAP_FACE",FACE,{"disambiguationData":[OSD([sQuery(id+"F0.wireOp",EDGE,"E0.sketch_text.stroke-0"),sQuery(id+"F0.wireOp",EDGE,"E0.sketch_text.stroke-1"),sQuery(id+"F0.wireOp",EDGE,"E0.sketch_text.stroke-2"),sQuery(id+"F0.wireOp",EDGE,"E0.sketch_text.stroke-3"),sQuery(id+"F0.wireOp",EDGE,"E0.sketch_text.stroke-4"),sQuery(id+"F0.wireOp",EDGE,"E0.sketch_text.stroke-5"),sQuery(id+"F0.wireOp",EDGE,"E0.sketch_text.stroke-6"),sQuery(id+"F0.wireOp",EDGE,"E0.sketch_text.stroke-7"),sQuery(id+"F0.wireOp",EDGE,"E0.sketch_text.stroke-8"),sQuery(id+"F0.wireOp",EDGE,"E0.sketch_text.stroke-9"),sQuery(id+"F0.wireOp",EDGE,"E0.sketch_text.stroke-10"),sQuery(id+"F0.wireOp",EDGE,"E0.sketch_text.stroke-11"),sQuery(id+"F0.wireOp",EDGE,"E0.sketch_text.stroke-12"),sQuery(id+"F0.wireOp",EDGE,"E0.sketch_text.stroke-13"),sQuery(id+"F0.wireOp",EDGE,"E0.sketch_text.stroke-14"),sQuery(id+"F0.wireOp",EDGE,"E0.sketch_text.stroke-15"),sQuery(id+"F0.wireOp",EDGE,"E0.sketch_text.stroke-16"),sQuery(id+"F0.wireOp",EDGE,"E0.sketch_text.stroke-17"),sQuery(id+"F0.wireOp",EDGE,"E0.sketch_text.stroke-18"),sQuery(id+"F0.wireOp",EDGE,"E0.sketch_text.stroke-19"),sQuery(id+"F0.wireOp",EDGE,"E0.sketch_text.stroke-20"),sQuery(id+"F0.wireOp",EDGE,"E0.sketch_text.stroke-21"),sQuery(id+"F0.wireOp",EDGE,"E0.sketch_text.stroke-22"),sQuery(id+"F0.wireOp",EDGE,"E0.sketch_text.stroke-23"),sQuery(id+"F0.wireOp",EDGE,"E0.sketch_text.stroke-24"),sQuery(id+"F0.wireOp",EDGE,"E0.sketch_text.stroke-33"),sQuery(id+"F0.wireOp",EDGE,"E0.sketch_text.stroke-34"),sQuery(id+"F0.wireOp",EDGE,"E0.sketch_text.stroke-35"),sQuery(id+"F0.wireOp",EDGE,"E0.sketch_text.stroke-36"),sQuery(id+"F0.wireOp",EDGE,"E0.sketch_text.stroke-37"),sQuery(id+"F0.wireOp",EDGE,"E0.sketch_text.stroke-38"),sQuery(id+"F0.wireOp",EDGE,"E0.sketch_text.stroke-39"),sQuery(id+"F0.wireOp",EDGE,"E0.sketch_text.stroke-40"),sQuery(id+"F0.wireOp",EDGE,"E0.sketch_text.stroke-41"),sQuery(id+"F0.wireOp",EDGE,"E0.sketch_text.stroke-42"),sQuery(id+"F0.wireOp",EDGE,"E0.sketch_text.stroke-43"),sQuery(id+"F0.wireOp",EDGE,"E0.sketch_text.stroke-44"),sQuery(id+"F0.wireOp",EDGE,"E0.sketch_text.stroke-45"),sQuery(id+"F0.wireOp",EDGE,"E0.sketch_text.stroke-46"),sQuery(id+"F0.wireOp",EDGE,"E0.sketch_text.stroke-47"),sQuery(id+"F0.wireOp",EDGE,"E0.sketch_text.stroke-48"),sQuery(id+"F0.wireOp",EDGE,"E0.sketch_text.stroke-49"),sQuery(id+"F0.wireOp",EDGE,"E0.sketch_text.stroke-50"),sQuery(id+"F0.wireOp",EDGE,"E0.sketch_text.stroke-51"),sQuery(id+"F0.wireOp",EDGE,"E0.sketch_text.stroke-52"),sQuery(id+"F0.wireOp",EDGE,"E0.sketch_text.stroke-53"),sQuery(id+"F0.wireOp",EDGE,"E0.sketch_text.stroke-54"),sQuery(id+"F0.wireOp",EDGE,"E0.sketch_text.stroke-55"),sQuery(id+"F0.wireOp",EDGE,"E0.sketch_text.stroke-56"),sQuery(id+"F0.wireOp",EDGE,"E0.sketch_text.stroke-57"),sQuery(id+"F0.wireOp",EDGE,"E0.sketch_text.stroke-58"),sQuery(id+"F0.wireOp",EDGE,"E0.sketch_text.stroke-59"),sQuery(id+"F0.wireOp",EDGE,"E0.sketch_text.stroke-60"),sQuery(id+"F0.wireOp",EDGE,"E0.sketch_text.stroke-61"),sQuery(id+"F0.wireOp",EDGE,"E0.sketch_text.stroke-62"),sQuery(id+"F0.wireOp",EDGE,"E0.sketch_text.stroke-63"),sQuery(id+"F0.wireOp",EDGE,"E0.sketch_text.stroke-64"),sQuery(id+"F0.wireOp",EDGE,"E0.sketch_text.stroke-65"),sQuery(id+"F0.wireOp",EDGE,"E0.sketch_text.stroke-66"),sQuery(id+"F0.wireOp",EDGE,"E0.sketch_text.stroke-67"),sQuery(id+"F0.wireOp",EDGE,"E0.sketch_text.stroke-68"),sQuery(id+"F0.wireOp",EDGE,"E0.sketch_text.stroke-69"),sQuery(id+"F0.wireOp",EDGE,"E0.sketch_text.stroke-70"),sQuery(id+"F0.wireOp",EDGE,"E0.sketch_text.stroke-71"),sQuery(id+"F0.wireOp",EDGE,"E0.sketch_text.stroke-72"),sQuery(id+"F0.wireOp",EDGE,"E0.sketch_text.stroke-73"),sQuery(id+"F0.wireOp",EDGE,"E0.sketch_text.stroke-74"),sQuery(id+"F0.wireOp",EDGE,"E0.sketch_text.stroke-75"),sQuery(id+"F0.wireOp",EDGE,"E0.sketch_text.stroke-76"),sQuery(id+"F0.wireOp",EDGE,"E0.sketch_text.stroke-77"),sQuery(id+"F0.wireOp",EDGE,"E0.sketch_text.stroke-78"),sQuery(id+"F0.wireOp",EDGE,"E0.sketch_text.stroke-79"),sQuery(id+"F0.wireOp",EDGE,"E0.sketch_text.stroke-80"),sQuery(id+"F0.wireOp",EDGE,"E0.sketch_text.stroke-81"),sQuery(id+"F0.wireOp",EDGE,"E1.bottom"),sQuery(id+"F0.wireOp",EDGE,"E1.top"),sQuery(id+"F0.wireOp",EDGE,"E1.left"),sQuery(id+"F0.wireOp",EDGE,"E1.right")])],"isStart":false})]});
            var Q2;
            Q2=makeQuery(id+"F4.boolean.opBoolean","INTERSECT",EDGE,{"derivedFrom":[makeQuery(id+"F2.opExtrude","CAP_FACE",FACE,{"disambiguationData":[OSD([sQuery(id+"F0.wireOp",EDGE,"E0.sketch_text.stroke-0"),sQuery(id+"F0.wireOp",EDGE,"E0.sketch_text.stroke-1"),sQuery(id+"F0.wireOp",EDGE,"E0.sketch_text.stroke-2"),sQuery(id+"F0.wireOp",EDGE,"E0.sketch_text.stroke-3"),sQuery(id+"F0.wireOp",EDGE,"E0.sketch_text.stroke-4"),sQuery(id+"F0.wireOp",EDGE,"E0.sketch_text.stroke-5"),sQuery(id+"F0.wireOp",EDGE,"E0.sketch_text.stroke-6"),sQuery(id+"F0.wireOp",EDGE,"E0.sketch_text.stroke-7"),sQuery(id+"F0.wireOp",EDGE,"E0.sketch_text.stroke-8"),sQuery(id+"F0.wireOp",EDGE,"E0.sketch_text.stroke-9"),sQuery(id+"F0.wireOp",EDGE,"E0.sketch_text.stroke-10"),sQuery(id+"F0.wireOp",EDGE,"E0.sketch_text.stroke-11"),sQuery(id+"F0.wireOp",EDGE,"E0.sketch_text.stroke-12"),sQuery(id+"F0.wireOp",EDGE,"E0.sketch_text.stroke-13"),sQuery(id+"F0.wireOp",EDGE,"E0.sketch_text.stroke-14"),sQuery(id+"F0.wireOp",EDGE,"E0.sketch_text.stroke-15"),sQuery(id+"F0.wireOp",EDGE,"E0.sketch_text.stroke-16"),sQuery(id+"F0.wireOp",EDGE,"E0.sketch_text.stroke-17"),sQuery(id+"F0.wireOp",EDGE,"E0.sketch_text.stroke-18"),sQuery(id+"F0.wireOp",EDGE,"E0.sketch_text.stroke-19"),sQuery(id+"F0.wireOp",EDGE,"E0.sketch_text.stroke-20"),sQuery(id+"F0.wireOp",EDGE,"E0.sketch_text.stroke-21"),sQuery(id+"F0.wireOp",EDGE,"E0.sketch_text.stroke-22"),sQuery(id+"F0.wireOp",EDGE,"E0.sketch_text.stroke-23"),sQuery(id+"F0.wireOp",EDGE,"E0.sketch_text.stroke-24"),sQuery(id+"F0.wireOp",EDGE,"E0.sketch_text.stroke-33"),sQuery(id+"F0.wireOp",EDGE,"E0.sketch_text.stroke-34"),sQuery(id+"F0.wireOp",EDGE,"E0.sketch_text.stroke-35"),sQuery(id+"F0.wireOp",EDGE,"E0.sketch_text.stroke-36"),sQuery(id+"F0.wireOp",EDGE,"E0.sketch_text.stroke-37"),sQuery(id+"F0.wireOp",EDGE,"E0.sketch_text.stroke-38"),sQuery(id+"F0.wireOp",EDGE,"E0.sketch_text.stroke-39"),sQuery(id+"F0.wireOp",EDGE,"E0.sketch_text.stroke-40"),sQuery(id+"F0.wireOp",EDGE,"E0.sketch_text.stroke-41"),sQuery(id+"F0.wireOp",EDGE,"E0.sketch_text.stroke-42"),sQuery(id+"F0.wireOp",EDGE,"E0.sketch_text.stroke-43"),sQuery(id+"F0.wireOp",EDGE,"E0.sketch_text.stroke-44"),sQuery(id+"F0.wireOp",EDGE,"E0.sketch_text.stroke-45"),sQuery(id+"F0.wireOp",EDGE,"E0.sketch_text.stroke-46"),sQuery(id+"F0.wireOp",EDGE,"E0.sketch_text.stroke-47"),sQuery(id+"F0.wireOp",EDGE,"E0.sketch_text.stroke-48"),sQuery(id+"F0.wireOp",EDGE,"E0.sketch_text.stroke-49"),sQuery(id+"F0.wireOp",EDGE,"E0.sketch_text.stroke-50"),sQuery(id+"F0.wireOp",EDGE,"E0.sketch_text.stroke-51"),sQuery(id+"F0.wireOp",EDGE,"E0.sketch_text.stroke-52"),sQuery(id+"F0.wireOp",EDGE,"E0.sketch_text.stroke-53"),sQuery(id+"F0.wireOp",EDGE,"E0.sketch_text.stroke-54"),sQuery(id+"F0.wireOp",EDGE,"E0.sketch_text.stroke-55"),sQuery(id+"F0.wireOp",EDGE,"E0.sketch_text.stroke-56"),sQuery(id+"F0.wireOp",EDGE,"E0.sketch_text.stroke-57"),sQuery(id+"F0.wireOp",EDGE,"E0.sketch_text.stroke-58"),sQuery(id+"F0.wireOp",EDGE,"E0.sketch_text.stroke-59"),sQuery(id+"F0.wireOp",EDGE,"E0.sketch_text.stroke-60"),sQuery(id+"F0.wireOp",EDGE,"E0.sketch_text.stroke-61"),sQuery(id+"F0.wireOp",EDGE,"E0.sketch_text.stroke-62"),sQuery(id+"F0.wireOp",EDGE,"E0.sketch_text.stroke-63"),sQuery(id+"F0.wireOp",EDGE,"E0.sketch_text.stroke-64"),sQuery(id+"F0.wireOp",EDGE,"E0.sketch_text.stroke-65"),sQuery(id+"F0.wireOp",EDGE,"E0.sketch_text.stroke-66"),sQuery(id+"F0.wireOp",EDGE,"E0.sketch_text.stroke-67"),sQuery(id+"F0.wireOp",EDGE,"E0.sketch_text.stroke-68"),sQuery(id+"F0.wireOp",EDGE,"E0.sketch_text.stroke-69"),sQuery(id+"F0.wireOp",EDGE,"E0.sketch_text.stroke-70"),sQuery(id+"F0.wireOp",EDGE,"E0.sketch_text.stroke-71"),sQuery(id+"F0.wireOp",EDGE,"E0.sketch_text.stroke-72"),sQuery(id+"F0.wireOp",EDGE,"E0.sketch_text.stroke-73"),sQuery(id+"F0.wireOp",EDGE,"E0.sketch_text.stroke-74"),sQuery(id+"F0.wireOp",EDGE,"E0.sketch_text.stroke-75"),sQuery(id+"F0.wireOp",EDGE,"E0.sketch_text.stroke-76"),sQuery(id+"F0.wireOp",EDGE,"E0.sketch_text.stroke-77"),sQuery(id+"F0.wireOp",EDGE,"E0.sketch_text.stroke-78"),sQuery(id+"F0.wireOp",EDGE,"E0.sketch_text.stroke-79"),sQuery(id+"F0.wireOp",EDGE,"E0.sketch_text.stroke-80"),sQuery(id+"F0.wireOp",EDGE,"E0.sketch_text.stroke-81"),sQuery(id+"F0.wireOp",EDGE,"E1.bottom"),sQuery(id+"F0.wireOp",EDGE,"E1.top"),sQuery(id+"F0.wireOp",EDGE,"E1.left"),sQuery(id+"F0.wireOp",EDGE,"E1.right")])],"isStart":false}),makeQuery(id+"F4.opExtrude","SWEPT_FACE",FACE,{"disambiguationData":[OSD([sQuery(id+"F3.wireOp",EDGE,"E5.1")])]})]});
            var Q3;
            Q3=makeQuery(id+"F5.opFillet","BLEND_EDGE",EDGE,{"blendedFrom":[makeQuery(id+"F4.boolean.opBoolean","COPY",EDGE,{"derivedFrom":makeQuery(id+"F4.opExtrude","SWEPT_EDGE",EDGE,{"disambiguationData":[OSD([sQuery(id+"F3.wireOp",EDGE,"E5.1"),sQuery(id+"F3.wireOp",EDGE,"E5.2")])]})}),makeQuery(id+"F2.opExtrude","CAP_FACE",FACE,{"disambiguationData":[OSD([sQuery(id+"F0.wireOp",EDGE,"E0.sketch_text.stroke-0"),sQuery(id+"F0.wireOp",EDGE,"E0.sketch_text.stroke-1"),sQuery(id+"F0.wireOp",EDGE,"E0.sketch_text.stroke-2"),sQuery(id+"F0.wireOp",EDGE,"E0.sketch_text.stroke-3"),sQuery(id+"F0.wireOp",EDGE,"E0.sketch_text.stroke-4"),sQuery(id+"F0.wireOp",EDGE,"E0.sketch_text.stroke-5"),sQuery(id+"F0.wireOp",EDGE,"E0.sketch_text.stroke-6"),sQuery(id+"F0.wireOp",EDGE,"E0.sketch_text.stroke-7"),sQuery(id+"F0.wireOp",EDGE,"E0.sketch_text.stroke-8"),sQuery(id+"F0.wireOp",EDGE,"E0.sketch_text.stroke-9"),sQuery(id+"F0.wireOp",EDGE,"E0.sketch_text.stroke-10"),sQuery(id+"F0.wireOp",EDGE,"E0.sketch_text.stroke-11"),sQuery(id+"F0.wireOp",EDGE,"E0.sketch_text.stroke-12"),sQuery(id+"F0.wireOp",EDGE,"E0.sketch_text.stroke-13"),sQuery(id+"F0.wireOp",EDGE,"E0.sketch_text.stroke-14"),sQuery(id+"F0.wireOp",EDGE,"E0.sketch_text.stroke-15"),sQuery(id+"F0.wireOp",EDGE,"E0.sketch_text.stroke-16"),sQuery(id+"F0.wireOp",EDGE,"E0.sketch_text.stroke-17"),sQuery(id+"F0.wireOp",EDGE,"E0.sketch_text.stroke-18"),sQuery(id+"F0.wireOp",EDGE,"E0.sketch_text.stroke-19"),sQuery(id+"F0.wireOp",EDGE,"E0.sketch_text.stroke-20"),sQuery(id+"F0.wireOp",EDGE,"E0.sketch_text.stroke-21"),sQuery(id+"F0.wireOp",EDGE,"E0.sketch_text.stroke-22"),sQuery(id+"F0.wireOp",EDGE,"E0.sketch_text.stroke-23"),sQuery(id+"F0.wireOp",EDGE,"E0.sketch_text.stroke-24"),sQuery(id+"F0.wireOp",EDGE,"E0.sketch_text.stroke-33"),sQuery(id+"F0.wireOp",EDGE,"E0.sketch_text.stroke-34"),sQuery(id+"F0.wireOp",EDGE,"E0.sketch_text.stroke-35"),sQuery(id+"F0.wireOp",EDGE,"E0.sketch_text.stroke-36"),sQuery(id+"F0.wireOp",EDGE,"E0.sketch_text.stroke-37"),sQuery(id+"F0.wireOp",EDGE,"E0.sketch_text.stroke-38"),sQuery(id+"F0.wireOp",EDGE,"E0.sketch_text.stroke-39"),sQuery(id+"F0.wireOp",EDGE,"E0.sketch_text.stroke-40"),sQuery(id+"F0.wireOp",EDGE,"E0.sketch_text.stroke-41"),sQuery(id+"F0.wireOp",EDGE,"E0.sketch_text.stroke-42"),sQuery(id+"F0.wireOp",EDGE,"E0.sketch_text.stroke-43"),sQuery(id+"F0.wireOp",EDGE,"E0.sketch_text.stroke-44"),sQuery(id+"F0.wireOp",EDGE,"E0.sketch_text.stroke-45"),sQuery(id+"F0.wireOp",EDGE,"E0.sketch_text.stroke-46"),sQuery(id+"F0.wireOp",EDGE,"E0.sketch_text.stroke-47"),sQuery(id+"F0.wireOp",EDGE,"E0.sketch_text.stroke-48"),sQuery(id+"F0.wireOp",EDGE,"E0.sketch_text.stroke-49"),sQuery(id+"F0.wireOp",EDGE,"E0.sketch_text.stroke-50"),sQuery(id+"F0.wireOp",EDGE,"E0.sketch_text.stroke-51"),sQuery(id+"F0.wireOp",EDGE,"E0.sketch_text.stroke-52"),sQuery(id+"F0.wireOp",EDGE,"E0.sketch_text.stroke-53"),sQuery(id+"F0.wireOp",EDGE,"E0.sketch_text.stroke-54"),sQuery(id+"F0.wireOp",EDGE,"E0.sketch_text.stroke-55"),sQuery(id+"F0.wireOp",EDGE,"E0.sketch_text.stroke-56"),sQuery(id+"F0.wireOp",EDGE,"E0.sketch_text.stroke-57"),sQuery(id+"F0.wireOp",EDGE,"E0.sketch_text.stroke-58"),sQuery(id+"F0.wireOp",EDGE,"E0.sketch_text.stroke-59"),sQuery(id+"F0.wireOp",EDGE,"E0.sketch_text.stroke-60"),sQuery(id+"F0.wireOp",EDGE,"E0.sketch_text.stroke-61"),sQuery(id+"F0.wireOp",EDGE,"E0.sketch_text.stroke-62"),sQuery(id+"F0.wireOp",EDGE,"E0.sketch_text.stroke-63"),sQuery(id+"F0.wireOp",EDGE,"E0.sketch_text.stroke-64"),sQuery(id+"F0.wireOp",EDGE,"E0.sketch_text.stroke-65"),sQuery(id+"F0.wireOp",EDGE,"E0.sketch_text.stroke-66"),sQuery(id+"F0.wireOp",EDGE,"E0.sketch_text.stroke-67"),sQuery(id+"F0.wireOp",EDGE,"E0.sketch_text.stroke-68"),sQuery(id+"F0.wireOp",EDGE,"E0.sketch_text.stroke-69"),sQuery(id+"F0.wireOp",EDGE,"E0.sketch_text.stroke-70"),sQuery(id+"F0.wireOp",EDGE,"E0.sketch_text.stroke-71"),sQuery(id+"F0.wireOp",EDGE,"E0.sketch_text.stroke-72"),sQuery(id+"F0.wireOp",EDGE,"E0.sketch_text.stroke-73"),sQuery(id+"F0.wireOp",EDGE,"E0.sketch_text.stroke-74"),sQuery(id+"F0.wireOp",EDGE,"E0.sketch_text.stroke-75"),sQuery(id+"F0.wireOp",EDGE,"E0.sketch_text.stroke-76"),sQuery(id+"F0.wireOp",EDGE,"E0.sketch_text.stroke-77"),sQuery(id+"F0.wireOp",EDGE,"E0.sketch_text.stroke-78"),sQuery(id+"F0.wireOp",EDGE,"E0.sketch_text.stroke-79"),sQuery(id+"F0.wireOp",EDGE,"E0.sketch_text.stroke-80"),sQuery(id+"F0.wireOp",EDGE,"E0.sketch_text.stroke-81"),sQuery(id+"F0.wireOp",EDGE,"E1.bottom"),sQuery(id+"F0.wireOp",EDGE,"E1.top"),sQuery(id+"F0.wireOp",EDGE,"E1.left"),sQuery(id+"F0.wireOp",EDGE,"E1.right")])],"isStart":false})],"blendedInto":[makeQuery(id+"F2.opExtrude","CAP_FACE",FACE,{"disambiguationData":[OSD([sQuery(id+"F0.wireOp",EDGE,"E0.sketch_text.stroke-0"),sQuery(id+"F0.wireOp",EDGE,"E0.sketch_text.stroke-1"),sQuery(id+"F0.wireOp",EDGE,"E0.sketch_text.stroke-2"),sQuery(id+"F0.wireOp",EDGE,"E0.sketch_text.stroke-3"),sQuery(id+"F0.wireOp",EDGE,"E0.sketch_text.stroke-4"),sQuery(id+"F0.wireOp",EDGE,"E0.sketch_text.stroke-5"),sQuery(id+"F0.wireOp",EDGE,"E0.sketch_text.stroke-6"),sQuery(id+"F0.wireOp",EDGE,"E0.sketch_text.stroke-7"),sQuery(id+"F0.wireOp",EDGE,"E0.sketch_text.stroke-8"),sQuery(id+"F0.wireOp",EDGE,"E0.sketch_text.stroke-9"),sQuery(id+"F0.wireOp",EDGE,"E0.sketch_text.stroke-10"),sQuery(id+"F0.wireOp",EDGE,"E0.sketch_text.stroke-11"),sQuery(id+"F0.wireOp",EDGE,"E0.sketch_text.stroke-12"),sQuery(id+"F0.wireOp",EDGE,"E0.sketch_text.stroke-13"),sQuery(id+"F0.wireOp",EDGE,"E0.sketch_text.stroke-14"),sQuery(id+"F0.wireOp",EDGE,"E0.sketch_text.stroke-15"),sQuery(id+"F0.wireOp",EDGE,"E0.sketch_text.stroke-16"),sQuery(id+"F0.wireOp",EDGE,"E0.sketch_text.stroke-17"),sQuery(id+"F0.wireOp",EDGE,"E0.sketch_text.stroke-18"),sQuery(id+"F0.wireOp",EDGE,"E0.sketch_text.stroke-19"),sQuery(id+"F0.wireOp",EDGE,"E0.sketch_text.stroke-20"),sQuery(id+"F0.wireOp",EDGE,"E0.sketch_text.stroke-21"),sQuery(id+"F0.wireOp",EDGE,"E0.sketch_text.stroke-22"),sQuery(id+"F0.wireOp",EDGE,"E0.sketch_text.stroke-23"),sQuery(id+"F0.wireOp",EDGE,"E0.sketch_text.stroke-24"),sQuery(id+"F0.wireOp",EDGE,"E0.sketch_text.stroke-33"),sQuery(id+"F0.wireOp",EDGE,"E0.sketch_text.stroke-34"),sQuery(id+"F0.wireOp",EDGE,"E0.sketch_text.stroke-35"),sQuery(id+"F0.wireOp",EDGE,"E0.sketch_text.stroke-36"),sQuery(id+"F0.wireOp",EDGE,"E0.sketch_text.stroke-37"),sQuery(id+"F0.wireOp",EDGE,"E0.sketch_text.stroke-38"),sQuery(id+"F0.wireOp",EDGE,"E0.sketch_text.stroke-39"),sQuery(id+"F0.wireOp",EDGE,"E0.sketch_text.stroke-40"),sQuery(id+"F0.wireOp",EDGE,"E0.sketch_text.stroke-41"),sQuery(id+"F0.wireOp",EDGE,"E0.sketch_text.stroke-42"),sQuery(id+"F0.wireOp",EDGE,"E0.sketch_text.stroke-43"),sQuery(id+"F0.wireOp",EDGE,"E0.sketch_text.stroke-44"),sQuery(id+"F0.wireOp",EDGE,"E0.sketch_text.stroke-45"),sQuery(id+"F0.wireOp",EDGE,"E0.sketch_text.stroke-46"),sQuery(id+"F0.wireOp",EDGE,"E0.sketch_text.stroke-47"),sQuery(id+"F0.wireOp",EDGE,"E0.sketch_text.stroke-48"),sQuery(id+"F0.wireOp",EDGE,"E0.sketch_text.stroke-49"),sQuery(id+"F0.wireOp",EDGE,"E0.sketch_text.stroke-50"),sQuery(id+"F0.wireOp",EDGE,"E0.sketch_text.stroke-51"),sQuery(id+"F0.wireOp",EDGE,"E0.sketch_text.stroke-52"),sQuery(id+"F0.wireOp",EDGE,"E0.sketch_text.stroke-53"),sQuery(id+"F0.wireOp",EDGE,"E0.sketch_text.stroke-54"),sQuery(id+"F0.wireOp",EDGE,"E0.sketch_text.stroke-55"),sQuery(id+"F0.wireOp",EDGE,"E0.sketch_text.stroke-56"),sQuery(id+"F0.wireOp",EDGE,"E0.sketch_text.stroke-57"),sQuery(id+"F0.wireOp",EDGE,"E0.sketch_text.stroke-58"),sQuery(id+"F0.wireOp",EDGE,"E0.sketch_text.stroke-59"),sQuery(id+"F0.wireOp",EDGE,"E0.sketch_text.stroke-60"),sQuery(id+"F0.wireOp",EDGE,"E0.sketch_text.stroke-61"),sQuery(id+"F0.wireOp",EDGE,"E0.sketch_text.stroke-62"),sQuery(id+"F0.wireOp",EDGE,"E0.sketch_text.stroke-63"),sQuery(id+"F0.wireOp",EDGE,"E0.sketch_text.stroke-64"),sQuery(id+"F0.wireOp",EDGE,"E0.sketch_text.stroke-65"),sQuery(id+"F0.wireOp",EDGE,"E0.sketch_text.stroke-66"),sQuery(id+"F0.wireOp",EDGE,"E0.sketch_text.stroke-67"),sQuery(id+"F0.wireOp",EDGE,"E0.sketch_text.stroke-68"),sQuery(id+"F0.wireOp",EDGE,"E0.sketch_text.stroke-69"),sQuery(id+"F0.wireOp",EDGE,"E0.sketch_text.stroke-70"),sQuery(id+"F0.wireOp",EDGE,"E0.sketch_text.stroke-71"),sQuery(id+"F0.wireOp",EDGE,"E0.sketch_text.stroke-72"),sQuery(id+"F0.wireOp",EDGE,"E0.sketch_text.stroke-73"),sQuery(id+"F0.wireOp",EDGE,"E0.sketch_text.stroke-74"),sQuery(id+"F0.wireOp",EDGE,"E0.sketch_text.stroke-75"),sQuery(id+"F0.wireOp",EDGE,"E0.sketch_text.stroke-76"),sQuery(id+"F0.wireOp",EDGE,"E0.sketch_text.stroke-77"),sQuery(id+"F0.wireOp",EDGE,"E0.sketch_text.stroke-78"),sQuery(id+"F0.wireOp",EDGE,"E0.sketch_text.stroke-79"),sQuery(id+"F0.wireOp",EDGE,"E0.sketch_text.stroke-80"),sQuery(id+"F0.wireOp",EDGE,"E0.sketch_text.stroke-81"),sQuery(id+"F0.wireOp",EDGE,"E1.bottom"),sQuery(id+"F0.wireOp",EDGE,"E1.top"),sQuery(id+"F0.wireOp",EDGE,"E1.left"),sQuery(id+"F0.wireOp",EDGE,"E1.right")])],"isStart":false})]});
            var Q4;
            Q4=makeQuery(id+"F4.boolean.opBoolean","INTERSECT",EDGE,{"derivedFrom":[makeQuery(id+"F2.opExtrude","CAP_FACE",FACE,{"disambiguationData":[OSD([sQuery(id+"F0.wireOp",EDGE,"E0.sketch_text.stroke-0"),sQuery(id+"F0.wireOp",EDGE,"E0.sketch_text.stroke-1"),sQuery(id+"F0.wireOp",EDGE,"E0.sketch_text.stroke-2"),sQuery(id+"F0.wireOp",EDGE,"E0.sketch_text.stroke-3"),sQuery(id+"F0.wireOp",EDGE,"E0.sketch_text.stroke-4"),sQuery(id+"F0.wireOp",EDGE,"E0.sketch_text.stroke-5"),sQuery(id+"F0.wireOp",EDGE,"E0.sketch_text.stroke-6"),sQuery(id+"F0.wireOp",EDGE,"E0.sketch_text.stroke-7"),sQuery(id+"F0.wireOp",EDGE,"E0.sketch_text.stroke-8"),sQuery(id+"F0.wireOp",EDGE,"E0.sketch_text.stroke-9"),sQuery(id+"F0.wireOp",EDGE,"E0.sketch_text.stroke-10"),sQuery(id+"F0.wireOp",EDGE,"E0.sketch_text.stroke-11"),sQuery(id+"F0.wireOp",EDGE,"E0.sketch_text.stroke-12"),sQuery(id+"F0.wireOp",EDGE,"E0.sketch_text.stroke-13"),sQuery(id+"F0.wireOp",EDGE,"E0.sketch_text.stroke-14"),sQuery(id+"F0.wireOp",EDGE,"E0.sketch_text.stroke-15"),sQuery(id+"F0.wireOp",EDGE,"E0.sketch_text.stroke-16"),sQuery(id+"F0.wireOp",EDGE,"E0.sketch_text.stroke-17"),sQuery(id+"F0.wireOp",EDGE,"E0.sketch_text.stroke-18"),sQuery(id+"F0.wireOp",EDGE,"E0.sketch_text.stroke-19"),sQuery(id+"F0.wireOp",EDGE,"E0.sketch_text.stroke-20"),sQuery(id+"F0.wireOp",EDGE,"E0.sketch_text.stroke-21"),sQuery(id+"F0.wireOp",EDGE,"E0.sketch_text.stroke-22"),sQuery(id+"F0.wireOp",EDGE,"E0.sketch_text.stroke-23"),sQuery(id+"F0.wireOp",EDGE,"E0.sketch_text.stroke-24"),sQuery(id+"F0.wireOp",EDGE,"E0.sketch_text.stroke-33"),sQuery(id+"F0.wireOp",EDGE,"E0.sketch_text.stroke-34"),sQuery(id+"F0.wireOp",EDGE,"E0.sketch_text.stroke-35"),sQuery(id+"F0.wireOp",EDGE,"E0.sketch_text.stroke-36"),sQuery(id+"F0.wireOp",EDGE,"E0.sketch_text.stroke-37"),sQuery(id+"F0.wireOp",EDGE,"E0.sketch_text.stroke-38"),sQuery(id+"F0.wireOp",EDGE,"E0.sketch_text.stroke-39"),sQuery(id+"F0.wireOp",EDGE,"E0.sketch_text.stroke-40"),sQuery(id+"F0.wireOp",EDGE,"E0.sketch_text.stroke-41"),sQuery(id+"F0.wireOp",EDGE,"E0.sketch_text.stroke-42"),sQuery(id+"F0.wireOp",EDGE,"E0.sketch_text.stroke-43"),sQuery(id+"F0.wireOp",EDGE,"E0.sketch_text.stroke-44"),sQuery(id+"F0.wireOp",EDGE,"E0.sketch_text.stroke-45"),sQuery(id+"F0.wireOp",EDGE,"E0.sketch_text.stroke-46"),sQuery(id+"F0.wireOp",EDGE,"E0.sketch_text.stroke-47"),sQuery(id+"F0.wireOp",EDGE,"E0.sketch_text.stroke-48"),sQuery(id+"F0.wireOp",EDGE,"E0.sketch_text.stroke-49"),sQuery(id+"F0.wireOp",EDGE,"E0.sketch_text.stroke-50"),sQuery(id+"F0.wireOp",EDGE,"E0.sketch_text.stroke-51"),sQuery(id+"F0.wireOp",EDGE,"E0.sketch_text.stroke-52"),sQuery(id+"F0.wireOp",EDGE,"E0.sketch_text.stroke-53"),sQuery(id+"F0.wireOp",EDGE,"E0.sketch_text.stroke-54"),sQuery(id+"F0.wireOp",EDGE,"E0.sketch_text.stroke-55"),sQuery(id+"F0.wireOp",EDGE,"E0.sketch_text.stroke-56"),sQuery(id+"F0.wireOp",EDGE,"E0.sketch_text.stroke-57"),sQuery(id+"F0.wireOp",EDGE,"E0.sketch_text.stroke-58"),sQuery(id+"F0.wireOp",EDGE,"E0.sketch_text.stroke-59"),sQuery(id+"F0.wireOp",EDGE,"E0.sketch_text.stroke-60"),sQuery(id+"F0.wireOp",EDGE,"E0.sketch_text.stroke-61"),sQuery(id+"F0.wireOp",EDGE,"E0.sketch_text.stroke-62"),sQuery(id+"F0.wireOp",EDGE,"E0.sketch_text.stroke-63"),sQuery(id+"F0.wireOp",EDGE,"E0.sketch_text.stroke-64"),sQuery(id+"F0.wireOp",EDGE,"E0.sketch_text.stroke-65"),sQuery(id+"F0.wireOp",EDGE,"E0.sketch_text.stroke-66"),sQuery(id+"F0.wireOp",EDGE,"E0.sketch_text.stroke-67"),sQuery(id+"F0.wireOp",EDGE,"E0.sketch_text.stroke-68"),sQuery(id+"F0.wireOp",EDGE,"E0.sketch_text.stroke-69"),sQuery(id+"F0.wireOp",EDGE,"E0.sketch_text.stroke-70"),sQuery(id+"F0.wireOp",EDGE,"E0.sketch_text.stroke-71"),sQuery(id+"F0.wireOp",EDGE,"E0.sketch_text.stroke-72"),sQuery(id+"F0.wireOp",EDGE,"E0.sketch_text.stroke-73"),sQuery(id+"F0.wireOp",EDGE,"E0.sketch_text.stroke-74"),sQuery(id+"F0.wireOp",EDGE,"E0.sketch_text.stroke-75"),sQuery(id+"F0.wireOp",EDGE,"E0.sketch_text.stroke-76"),sQuery(id+"F0.wireOp",EDGE,"E0.sketch_text.stroke-77"),sQuery(id+"F0.wireOp",EDGE,"E0.sketch_text.stroke-78"),sQuery(id+"F0.wireOp",EDGE,"E0.sketch_text.stroke-79"),sQuery(id+"F0.wireOp",EDGE,"E0.sketch_text.stroke-80"),sQuery(id+"F0.wireOp",EDGE,"E0.sketch_text.stroke-81"),sQuery(id+"F0.wireOp",EDGE,"E1.bottom"),sQuery(id+"F0.wireOp",EDGE,"E1.top"),sQuery(id+"F0.wireOp",EDGE,"E1.left"),sQuery(id+"F0.wireOp",EDGE,"E1.right")])],"isStart":false}),makeQuery(id+"F4.opExtrude","SWEPT_FACE",FACE,{"disambiguationData":[OSD([sQuery(id+"F3.wireOp",EDGE,"E5.2")])]})]});
            var Q5;
            Q5=makeQuery(id+"F5.opFillet","BLEND_EDGE",EDGE,{"blendedFrom":[makeQuery(id+"F4.boolean.opBoolean","COPY",EDGE,{"derivedFrom":makeQuery(id+"F4.opExtrude","SWEPT_EDGE",EDGE,{"disambiguationData":[OSD([sQuery(id+"F3.wireOp",EDGE,"E5.2"),sQuery(id+"F3.wireOp",EDGE,"E8")])]})}),makeQuery(id+"F2.opExtrude","CAP_FACE",FACE,{"disambiguationData":[OSD([sQuery(id+"F0.wireOp",EDGE,"E0.sketch_text.stroke-0"),sQuery(id+"F0.wireOp",EDGE,"E0.sketch_text.stroke-1"),sQuery(id+"F0.wireOp",EDGE,"E0.sketch_text.stroke-2"),sQuery(id+"F0.wireOp",EDGE,"E0.sketch_text.stroke-3"),sQuery(id+"F0.wireOp",EDGE,"E0.sketch_text.stroke-4"),sQuery(id+"F0.wireOp",EDGE,"E0.sketch_text.stroke-5"),sQuery(id+"F0.wireOp",EDGE,"E0.sketch_text.stroke-6"),sQuery(id+"F0.wireOp",EDGE,"E0.sketch_text.stroke-7"),sQuery(id+"F0.wireOp",EDGE,"E0.sketch_text.stroke-8"),sQuery(id+"F0.wireOp",EDGE,"E0.sketch_text.stroke-9"),sQuery(id+"F0.wireOp",EDGE,"E0.sketch_text.stroke-10"),sQuery(id+"F0.wireOp",EDGE,"E0.sketch_text.stroke-11"),sQuery(id+"F0.wireOp",EDGE,"E0.sketch_text.stroke-12"),sQuery(id+"F0.wireOp",EDGE,"E0.sketch_text.stroke-13"),sQuery(id+"F0.wireOp",EDGE,"E0.sketch_text.stroke-14"),sQuery(id+"F0.wireOp",EDGE,"E0.sketch_text.stroke-15"),sQuery(id+"F0.wireOp",EDGE,"E0.sketch_text.stroke-16"),sQuery(id+"F0.wireOp",EDGE,"E0.sketch_text.stroke-17"),sQuery(id+"F0.wireOp",EDGE,"E0.sketch_text.stroke-18"),sQuery(id+"F0.wireOp",EDGE,"E0.sketch_text.stroke-19"),sQuery(id+"F0.wireOp",EDGE,"E0.sketch_text.stroke-20"),sQuery(id+"F0.wireOp",EDGE,"E0.sketch_text.stroke-21"),sQuery(id+"F0.wireOp",EDGE,"E0.sketch_text.stroke-22"),sQuery(id+"F0.wireOp",EDGE,"E0.sketch_text.stroke-23"),sQuery(id+"F0.wireOp",EDGE,"E0.sketch_text.stroke-24"),sQuery(id+"F0.wireOp",EDGE,"E0.sketch_text.stroke-33"),sQuery(id+"F0.wireOp",EDGE,"E0.sketch_text.stroke-34"),sQuery(id+"F0.wireOp",EDGE,"E0.sketch_text.stroke-35"),sQuery(id+"F0.wireOp",EDGE,"E0.sketch_text.stroke-36"),sQuery(id+"F0.wireOp",EDGE,"E0.sketch_text.stroke-37"),sQuery(id+"F0.wireOp",EDGE,"E0.sketch_text.stroke-38"),sQuery(id+"F0.wireOp",EDGE,"E0.sketch_text.stroke-39"),sQuery(id+"F0.wireOp",EDGE,"E0.sketch_text.stroke-40"),sQuery(id+"F0.wireOp",EDGE,"E0.sketch_text.stroke-41"),sQuery(id+"F0.wireOp",EDGE,"E0.sketch_text.stroke-42"),sQuery(id+"F0.wireOp",EDGE,"E0.sketch_text.stroke-43"),sQuery(id+"F0.wireOp",EDGE,"E0.sketch_text.stroke-44"),sQuery(id+"F0.wireOp",EDGE,"E0.sketch_text.stroke-45"),sQuery(id+"F0.wireOp",EDGE,"E0.sketch_text.stroke-46"),sQuery(id+"F0.wireOp",EDGE,"E0.sketch_text.stroke-47"),sQuery(id+"F0.wireOp",EDGE,"E0.sketch_text.stroke-48"),sQuery(id+"F0.wireOp",EDGE,"E0.sketch_text.stroke-49"),sQuery(id+"F0.wireOp",EDGE,"E0.sketch_text.stroke-50"),sQuery(id+"F0.wireOp",EDGE,"E0.sketch_text.stroke-51"),sQuery(id+"F0.wireOp",EDGE,"E0.sketch_text.stroke-52"),sQuery(id+"F0.wireOp",EDGE,"E0.sketch_text.stroke-53"),sQuery(id+"F0.wireOp",EDGE,"E0.sketch_text.stroke-54"),sQuery(id+"F0.wireOp",EDGE,"E0.sketch_text.stroke-55"),sQuery(id+"F0.wireOp",EDGE,"E0.sketch_text.stroke-56"),sQuery(id+"F0.wireOp",EDGE,"E0.sketch_text.stroke-57"),sQuery(id+"F0.wireOp",EDGE,"E0.sketch_text.stroke-58"),sQuery(id+"F0.wireOp",EDGE,"E0.sketch_text.stroke-59"),sQuery(id+"F0.wireOp",EDGE,"E0.sketch_text.stroke-60"),sQuery(id+"F0.wireOp",EDGE,"E0.sketch_text.stroke-61"),sQuery(id+"F0.wireOp",EDGE,"E0.sketch_text.stroke-62"),sQuery(id+"F0.wireOp",EDGE,"E0.sketch_text.stroke-63"),sQuery(id+"F0.wireOp",EDGE,"E0.sketch_text.stroke-64"),sQuery(id+"F0.wireOp",EDGE,"E0.sketch_text.stroke-65"),sQuery(id+"F0.wireOp",EDGE,"E0.sketch_text.stroke-66"),sQuery(id+"F0.wireOp",EDGE,"E0.sketch_text.stroke-67"),sQuery(id+"F0.wireOp",EDGE,"E0.sketch_text.stroke-68"),sQuery(id+"F0.wireOp",EDGE,"E0.sketch_text.stroke-69"),sQuery(id+"F0.wireOp",EDGE,"E0.sketch_text.stroke-70"),sQuery(id+"F0.wireOp",EDGE,"E0.sketch_text.stroke-71"),sQuery(id+"F0.wireOp",EDGE,"E0.sketch_text.stroke-72"),sQuery(id+"F0.wireOp",EDGE,"E0.sketch_text.stroke-73"),sQuery(id+"F0.wireOp",EDGE,"E0.sketch_text.stroke-74"),sQuery(id+"F0.wireOp",EDGE,"E0.sketch_text.stroke-75"),sQuery(id+"F0.wireOp",EDGE,"E0.sketch_text.stroke-76"),sQuery(id+"F0.wireOp",EDGE,"E0.sketch_text.stroke-77"),sQuery(id+"F0.wireOp",EDGE,"E0.sketch_text.stroke-78"),sQuery(id+"F0.wireOp",EDGE,"E0.sketch_text.stroke-79"),sQuery(id+"F0.wireOp",EDGE,"E0.sketch_text.stroke-80"),sQuery(id+"F0.wireOp",EDGE,"E0.sketch_text.stroke-81"),sQuery(id+"F0.wireOp",EDGE,"E1.bottom"),sQuery(id+"F0.wireOp",EDGE,"E1.top"),sQuery(id+"F0.wireOp",EDGE,"E1.left"),sQuery(id+"F0.wireOp",EDGE,"E1.right")])],"isStart":false})],"blendedInto":[makeQuery(id+"F2.opExtrude","CAP_FACE",FACE,{"disambiguationData":[OSD([sQuery(id+"F0.wireOp",EDGE,"E0.sketch_text.stroke-0"),sQuery(id+"F0.wireOp",EDGE,"E0.sketch_text.stroke-1"),sQuery(id+"F0.wireOp",EDGE,"E0.sketch_text.stroke-2"),sQuery(id+"F0.wireOp",EDGE,"E0.sketch_text.stroke-3"),sQuery(id+"F0.wireOp",EDGE,"E0.sketch_text.stroke-4"),sQuery(id+"F0.wireOp",EDGE,"E0.sketch_text.stroke-5"),sQuery(id+"F0.wireOp",EDGE,"E0.sketch_text.stroke-6"),sQuery(id+"F0.wireOp",EDGE,"E0.sketch_text.stroke-7"),sQuery(id+"F0.wireOp",EDGE,"E0.sketch_text.stroke-8"),sQuery(id+"F0.wireOp",EDGE,"E0.sketch_text.stroke-9"),sQuery(id+"F0.wireOp",EDGE,"E0.sketch_text.stroke-10"),sQuery(id+"F0.wireOp",EDGE,"E0.sketch_text.stroke-11"),sQuery(id+"F0.wireOp",EDGE,"E0.sketch_text.stroke-12"),sQuery(id+"F0.wireOp",EDGE,"E0.sketch_text.stroke-13"),sQuery(id+"F0.wireOp",EDGE,"E0.sketch_text.stroke-14"),sQuery(id+"F0.wireOp",EDGE,"E0.sketch_text.stroke-15"),sQuery(id+"F0.wireOp",EDGE,"E0.sketch_text.stroke-16"),sQuery(id+"F0.wireOp",EDGE,"E0.sketch_text.stroke-17"),sQuery(id+"F0.wireOp",EDGE,"E0.sketch_text.stroke-18"),sQuery(id+"F0.wireOp",EDGE,"E0.sketch_text.stroke-19"),sQuery(id+"F0.wireOp",EDGE,"E0.sketch_text.stroke-20"),sQuery(id+"F0.wireOp",EDGE,"E0.sketch_text.stroke-21"),sQuery(id+"F0.wireOp",EDGE,"E0.sketch_text.stroke-22"),sQuery(id+"F0.wireOp",EDGE,"E0.sketch_text.stroke-23"),sQuery(id+"F0.wireOp",EDGE,"E0.sketch_text.stroke-24"),sQuery(id+"F0.wireOp",EDGE,"E0.sketch_text.stroke-33"),sQuery(id+"F0.wireOp",EDGE,"E0.sketch_text.stroke-34"),sQuery(id+"F0.wireOp",EDGE,"E0.sketch_text.stroke-35"),sQuery(id+"F0.wireOp",EDGE,"E0.sketch_text.stroke-36"),sQuery(id+"F0.wireOp",EDGE,"E0.sketch_text.stroke-37"),sQuery(id+"F0.wireOp",EDGE,"E0.sketch_text.stroke-38"),sQuery(id+"F0.wireOp",EDGE,"E0.sketch_text.stroke-39"),sQuery(id+"F0.wireOp",EDGE,"E0.sketch_text.stroke-40"),sQuery(id+"F0.wireOp",EDGE,"E0.sketch_text.stroke-41"),sQuery(id+"F0.wireOp",EDGE,"E0.sketch_text.stroke-42"),sQuery(id+"F0.wireOp",EDGE,"E0.sketch_text.stroke-43"),sQuery(id+"F0.wireOp",EDGE,"E0.sketch_text.stroke-44"),sQuery(id+"F0.wireOp",EDGE,"E0.sketch_text.stroke-45"),sQuery(id+"F0.wireOp",EDGE,"E0.sketch_text.stroke-46"),sQuery(id+"F0.wireOp",EDGE,"E0.sketch_text.stroke-47"),sQuery(id+"F0.wireOp",EDGE,"E0.sketch_text.stroke-48"),sQuery(id+"F0.wireOp",EDGE,"E0.sketch_text.stroke-49"),sQuery(id+"F0.wireOp",EDGE,"E0.sketch_text.stroke-50"),sQuery(id+"F0.wireOp",EDGE,"E0.sketch_text.stroke-51"),sQuery(id+"F0.wireOp",EDGE,"E0.sketch_text.stroke-52"),sQuery(id+"F0.wireOp",EDGE,"E0.sketch_text.stroke-53"),sQuery(id+"F0.wireOp",EDGE,"E0.sketch_text.stroke-54"),sQuery(id+"F0.wireOp",EDGE,"E0.sketch_text.stroke-55"),sQuery(id+"F0.wireOp",EDGE,"E0.sketch_text.stroke-56"),sQuery(id+"F0.wireOp",EDGE,"E0.sketch_text.stroke-57"),sQuery(id+"F0.wireOp",EDGE,"E0.sketch_text.stroke-58"),sQuery(id+"F0.wireOp",EDGE,"E0.sketch_text.stroke-59"),sQuery(id+"F0.wireOp",EDGE,"E0.sketch_text.stroke-60"),sQuery(id+"F0.wireOp",EDGE,"E0.sketch_text.stroke-61"),sQuery(id+"F0.wireOp",EDGE,"E0.sketch_text.stroke-62"),sQuery(id+"F0.wireOp",EDGE,"E0.sketch_text.stroke-63"),sQuery(id+"F0.wireOp",EDGE,"E0.sketch_text.stroke-64"),sQuery(id+"F0.wireOp",EDGE,"E0.sketch_text.stroke-65"),sQuery(id+"F0.wireOp",EDGE,"E0.sketch_text.stroke-66"),sQuery(id+"F0.wireOp",EDGE,"E0.sketch_text.stroke-67"),sQuery(id+"F0.wireOp",EDGE,"E0.sketch_text.stroke-68"),sQuery(id+"F0.wireOp",EDGE,"E0.sketch_text.stroke-69"),sQuery(id+"F0.wireOp",EDGE,"E0.sketch_text.stroke-70"),sQuery(id+"F0.wireOp",EDGE,"E0.sketch_text.stroke-71"),sQuery(id+"F0.wireOp",EDGE,"E0.sketch_text.stroke-72"),sQuery(id+"F0.wireOp",EDGE,"E0.sketch_text.stroke-73"),sQuery(id+"F0.wireOp",EDGE,"E0.sketch_text.stroke-74"),sQuery(id+"F0.wireOp",EDGE,"E0.sketch_text.stroke-75"),sQuery(id+"F0.wireOp",EDGE,"E0.sketch_text.stroke-76"),sQuery(id+"F0.wireOp",EDGE,"E0.sketch_text.stroke-77"),sQuery(id+"F0.wireOp",EDGE,"E0.sketch_text.stroke-78"),sQuery(id+"F0.wireOp",EDGE,"E0.sketch_text.stroke-79"),sQuery(id+"F0.wireOp",EDGE,"E0.sketch_text.stroke-80"),sQuery(id+"F0.wireOp",EDGE,"E0.sketch_text.stroke-81"),sQuery(id+"F0.wireOp",EDGE,"E1.bottom"),sQuery(id+"F0.wireOp",EDGE,"E1.top"),sQuery(id+"F0.wireOp",EDGE,"E1.left"),sQuery(id+"F0.wireOp",EDGE,"E1.right")])],"isStart":false})]});
            var Q6;
            Q6=makeQuery(id+"F6.opFillet","BLEND_EDGE",EDGE,{"blendedFrom":[makeQuery(id+"F4.boolean.opBoolean","COPY",EDGE,{"derivedFrom":makeQuery(id+"F4.opExtrude","SWEPT_EDGE",EDGE,{"disambiguationData":[OSD([sQuery(id+"F3.wireOp",EDGE,"E7"),sQuery(id+"F3.wireOp",EDGE,"E8")])]})}),makeQuery(id+"F2.opExtrude","CAP_FACE",FACE,{"disambiguationData":[OSD([sQuery(id+"F0.wireOp",EDGE,"E0.sketch_text.stroke-0"),sQuery(id+"F0.wireOp",EDGE,"E0.sketch_text.stroke-1"),sQuery(id+"F0.wireOp",EDGE,"E0.sketch_text.stroke-2"),sQuery(id+"F0.wireOp",EDGE,"E0.sketch_text.stroke-3"),sQuery(id+"F0.wireOp",EDGE,"E0.sketch_text.stroke-4"),sQuery(id+"F0.wireOp",EDGE,"E0.sketch_text.stroke-5"),sQuery(id+"F0.wireOp",EDGE,"E0.sketch_text.stroke-6"),sQuery(id+"F0.wireOp",EDGE,"E0.sketch_text.stroke-7"),sQuery(id+"F0.wireOp",EDGE,"E0.sketch_text.stroke-8"),sQuery(id+"F0.wireOp",EDGE,"E0.sketch_text.stroke-9"),sQuery(id+"F0.wireOp",EDGE,"E0.sketch_text.stroke-10"),sQuery(id+"F0.wireOp",EDGE,"E0.sketch_text.stroke-11"),sQuery(id+"F0.wireOp",EDGE,"E0.sketch_text.stroke-12"),sQuery(id+"F0.wireOp",EDGE,"E0.sketch_text.stroke-13"),sQuery(id+"F0.wireOp",EDGE,"E0.sketch_text.stroke-14"),sQuery(id+"F0.wireOp",EDGE,"E0.sketch_text.stroke-15"),sQuery(id+"F0.wireOp",EDGE,"E0.sketch_text.stroke-16"),sQuery(id+"F0.wireOp",EDGE,"E0.sketch_text.stroke-17"),sQuery(id+"F0.wireOp",EDGE,"E0.sketch_text.stroke-18"),sQuery(id+"F0.wireOp",EDGE,"E0.sketch_text.stroke-19"),sQuery(id+"F0.wireOp",EDGE,"E0.sketch_text.stroke-20"),sQuery(id+"F0.wireOp",EDGE,"E0.sketch_text.stroke-21"),sQuery(id+"F0.wireOp",EDGE,"E0.sketch_text.stroke-22"),sQuery(id+"F0.wireOp",EDGE,"E0.sketch_text.stroke-23"),sQuery(id+"F0.wireOp",EDGE,"E0.sketch_text.stroke-24"),sQuery(id+"F0.wireOp",EDGE,"E0.sketch_text.stroke-33"),sQuery(id+"F0.wireOp",EDGE,"E0.sketch_text.stroke-34"),sQuery(id+"F0.wireOp",EDGE,"E0.sketch_text.stroke-35"),sQuery(id+"F0.wireOp",EDGE,"E0.sketch_text.stroke-36"),sQuery(id+"F0.wireOp",EDGE,"E0.sketch_text.stroke-37"),sQuery(id+"F0.wireOp",EDGE,"E0.sketch_text.stroke-38"),sQuery(id+"F0.wireOp",EDGE,"E0.sketch_text.stroke-39"),sQuery(id+"F0.wireOp",EDGE,"E0.sketch_text.stroke-40"),sQuery(id+"F0.wireOp",EDGE,"E0.sketch_text.stroke-41"),sQuery(id+"F0.wireOp",EDGE,"E0.sketch_text.stroke-42"),sQuery(id+"F0.wireOp",EDGE,"E0.sketch_text.stroke-43"),sQuery(id+"F0.wireOp",EDGE,"E0.sketch_text.stroke-44"),sQuery(id+"F0.wireOp",EDGE,"E0.sketch_text.stroke-45"),sQuery(id+"F0.wireOp",EDGE,"E0.sketch_text.stroke-46"),sQuery(id+"F0.wireOp",EDGE,"E0.sketch_text.stroke-47"),sQuery(id+"F0.wireOp",EDGE,"E0.sketch_text.stroke-48"),sQuery(id+"F0.wireOp",EDGE,"E0.sketch_text.stroke-49"),sQuery(id+"F0.wireOp",EDGE,"E0.sketch_text.stroke-50"),sQuery(id+"F0.wireOp",EDGE,"E0.sketch_text.stroke-51"),sQuery(id+"F0.wireOp",EDGE,"E0.sketch_text.stroke-52"),sQuery(id+"F0.wireOp",EDGE,"E0.sketch_text.stroke-53"),sQuery(id+"F0.wireOp",EDGE,"E0.sketch_text.stroke-54"),sQuery(id+"F0.wireOp",EDGE,"E0.sketch_text.stroke-55"),sQuery(id+"F0.wireOp",EDGE,"E0.sketch_text.stroke-56"),sQuery(id+"F0.wireOp",EDGE,"E0.sketch_text.stroke-57"),sQuery(id+"F0.wireOp",EDGE,"E0.sketch_text.stroke-58"),sQuery(id+"F0.wireOp",EDGE,"E0.sketch_text.stroke-59"),sQuery(id+"F0.wireOp",EDGE,"E0.sketch_text.stroke-60"),sQuery(id+"F0.wireOp",EDGE,"E0.sketch_text.stroke-61"),sQuery(id+"F0.wireOp",EDGE,"E0.sketch_text.stroke-62"),sQuery(id+"F0.wireOp",EDGE,"E0.sketch_text.stroke-63"),sQuery(id+"F0.wireOp",EDGE,"E0.sketch_text.stroke-64"),sQuery(id+"F0.wireOp",EDGE,"E0.sketch_text.stroke-65"),sQuery(id+"F0.wireOp",EDGE,"E0.sketch_text.stroke-66"),sQuery(id+"F0.wireOp",EDGE,"E0.sketch_text.stroke-67"),sQuery(id+"F0.wireOp",EDGE,"E0.sketch_text.stroke-68"),sQuery(id+"F0.wireOp",EDGE,"E0.sketch_text.stroke-69"),sQuery(id+"F0.wireOp",EDGE,"E0.sketch_text.stroke-70"),sQuery(id+"F0.wireOp",EDGE,"E0.sketch_text.stroke-71"),sQuery(id+"F0.wireOp",EDGE,"E0.sketch_text.stroke-72"),sQuery(id+"F0.wireOp",EDGE,"E0.sketch_text.stroke-73"),sQuery(id+"F0.wireOp",EDGE,"E0.sketch_text.stroke-74"),sQuery(id+"F0.wireOp",EDGE,"E0.sketch_text.stroke-75"),sQuery(id+"F0.wireOp",EDGE,"E0.sketch_text.stroke-76"),sQuery(id+"F0.wireOp",EDGE,"E0.sketch_text.stroke-77"),sQuery(id+"F0.wireOp",EDGE,"E0.sketch_text.stroke-78"),sQuery(id+"F0.wireOp",EDGE,"E0.sketch_text.stroke-79"),sQuery(id+"F0.wireOp",EDGE,"E0.sketch_text.stroke-80"),sQuery(id+"F0.wireOp",EDGE,"E0.sketch_text.stroke-81"),sQuery(id+"F0.wireOp",EDGE,"E1.bottom"),sQuery(id+"F0.wireOp",EDGE,"E1.top"),sQuery(id+"F0.wireOp",EDGE,"E1.left"),sQuery(id+"F0.wireOp",EDGE,"E1.right")])],"isStart":false})],"blendedInto":[makeQuery(id+"F2.opExtrude","CAP_FACE",FACE,{"disambiguationData":[OSD([sQuery(id+"F0.wireOp",EDGE,"E0.sketch_text.stroke-0"),sQuery(id+"F0.wireOp",EDGE,"E0.sketch_text.stroke-1"),sQuery(id+"F0.wireOp",EDGE,"E0.sketch_text.stroke-2"),sQuery(id+"F0.wireOp",EDGE,"E0.sketch_text.stroke-3"),sQuery(id+"F0.wireOp",EDGE,"E0.sketch_text.stroke-4"),sQuery(id+"F0.wireOp",EDGE,"E0.sketch_text.stroke-5"),sQuery(id+"F0.wireOp",EDGE,"E0.sketch_text.stroke-6"),sQuery(id+"F0.wireOp",EDGE,"E0.sketch_text.stroke-7"),sQuery(id+"F0.wireOp",EDGE,"E0.sketch_text.stroke-8"),sQuery(id+"F0.wireOp",EDGE,"E0.sketch_text.stroke-9"),sQuery(id+"F0.wireOp",EDGE,"E0.sketch_text.stroke-10"),sQuery(id+"F0.wireOp",EDGE,"E0.sketch_text.stroke-11"),sQuery(id+"F0.wireOp",EDGE,"E0.sketch_text.stroke-12"),sQuery(id+"F0.wireOp",EDGE,"E0.sketch_text.stroke-13"),sQuery(id+"F0.wireOp",EDGE,"E0.sketch_text.stroke-14"),sQuery(id+"F0.wireOp",EDGE,"E0.sketch_text.stroke-15"),sQuery(id+"F0.wireOp",EDGE,"E0.sketch_text.stroke-16"),sQuery(id+"F0.wireOp",EDGE,"E0.sketch_text.stroke-17"),sQuery(id+"F0.wireOp",EDGE,"E0.sketch_text.stroke-18"),sQuery(id+"F0.wireOp",EDGE,"E0.sketch_text.stroke-19"),sQuery(id+"F0.wireOp",EDGE,"E0.sketch_text.stroke-20"),sQuery(id+"F0.wireOp",EDGE,"E0.sketch_text.stroke-21"),sQuery(id+"F0.wireOp",EDGE,"E0.sketch_text.stroke-22"),sQuery(id+"F0.wireOp",EDGE,"E0.sketch_text.stroke-23"),sQuery(id+"F0.wireOp",EDGE,"E0.sketch_text.stroke-24"),sQuery(id+"F0.wireOp",EDGE,"E0.sketch_text.stroke-33"),sQuery(id+"F0.wireOp",EDGE,"E0.sketch_text.stroke-34"),sQuery(id+"F0.wireOp",EDGE,"E0.sketch_text.stroke-35"),sQuery(id+"F0.wireOp",EDGE,"E0.sketch_text.stroke-36"),sQuery(id+"F0.wireOp",EDGE,"E0.sketch_text.stroke-37"),sQuery(id+"F0.wireOp",EDGE,"E0.sketch_text.stroke-38"),sQuery(id+"F0.wireOp",EDGE,"E0.sketch_text.stroke-39"),sQuery(id+"F0.wireOp",EDGE,"E0.sketch_text.stroke-40"),sQuery(id+"F0.wireOp",EDGE,"E0.sketch_text.stroke-41"),sQuery(id+"F0.wireOp",EDGE,"E0.sketch_text.stroke-42"),sQuery(id+"F0.wireOp",EDGE,"E0.sketch_text.stroke-43"),sQuery(id+"F0.wireOp",EDGE,"E0.sketch_text.stroke-44"),sQuery(id+"F0.wireOp",EDGE,"E0.sketch_text.stroke-45"),sQuery(id+"F0.wireOp",EDGE,"E0.sketch_text.stroke-46"),sQuery(id+"F0.wireOp",EDGE,"E0.sketch_text.stroke-47"),sQuery(id+"F0.wireOp",EDGE,"E0.sketch_text.stroke-48"),sQuery(id+"F0.wireOp",EDGE,"E0.sketch_text.stroke-49"),sQuery(id+"F0.wireOp",EDGE,"E0.sketch_text.stroke-50"),sQuery(id+"F0.wireOp",EDGE,"E0.sketch_text.stroke-51"),sQuery(id+"F0.wireOp",EDGE,"E0.sketch_text.stroke-52"),sQuery(id+"F0.wireOp",EDGE,"E0.sketch_text.stroke-53"),sQuery(id+"F0.wireOp",EDGE,"E0.sketch_text.stroke-54"),sQuery(id+"F0.wireOp",EDGE,"E0.sketch_text.stroke-55"),sQuery(id+"F0.wireOp",EDGE,"E0.sketch_text.stroke-56"),sQuery(id+"F0.wireOp",EDGE,"E0.sketch_text.stroke-57"),sQuery(id+"F0.wireOp",EDGE,"E0.sketch_text.stroke-58"),sQuery(id+"F0.wireOp",EDGE,"E0.sketch_text.stroke-59"),sQuery(id+"F0.wireOp",EDGE,"E0.sketch_text.stroke-60"),sQuery(id+"F0.wireOp",EDGE,"E0.sketch_text.stroke-61"),sQuery(id+"F0.wireOp",EDGE,"E0.sketch_text.stroke-62"),sQuery(id+"F0.wireOp",EDGE,"E0.sketch_text.stroke-63"),sQuery(id+"F0.wireOp",EDGE,"E0.sketch_text.stroke-64"),sQuery(id+"F0.wireOp",EDGE,"E0.sketch_text.stroke-65"),sQuery(id+"F0.wireOp",EDGE,"E0.sketch_text.stroke-66"),sQuery(id+"F0.wireOp",EDGE,"E0.sketch_text.stroke-67"),sQuery(id+"F0.wireOp",EDGE,"E0.sketch_text.stroke-68"),sQuery(id+"F0.wireOp",EDGE,"E0.sketch_text.stroke-69"),sQuery(id+"F0.wireOp",EDGE,"E0.sketch_text.stroke-70"),sQuery(id+"F0.wireOp",EDGE,"E0.sketch_text.stroke-71"),sQuery(id+"F0.wireOp",EDGE,"E0.sketch_text.stroke-72"),sQuery(id+"F0.wireOp",EDGE,"E0.sketch_text.stroke-73"),sQuery(id+"F0.wireOp",EDGE,"E0.sketch_text.stroke-74"),sQuery(id+"F0.wireOp",EDGE,"E0.sketch_text.stroke-75"),sQuery(id+"F0.wireOp",EDGE,"E0.sketch_text.stroke-76"),sQuery(id+"F0.wireOp",EDGE,"E0.sketch_text.stroke-77"),sQuery(id+"F0.wireOp",EDGE,"E0.sketch_text.stroke-78"),sQuery(id+"F0.wireOp",EDGE,"E0.sketch_text.stroke-79"),sQuery(id+"F0.wireOp",EDGE,"E0.sketch_text.stroke-80"),sQuery(id+"F0.wireOp",EDGE,"E0.sketch_text.stroke-81"),sQuery(id+"F0.wireOp",EDGE,"E1.bottom"),sQuery(id+"F0.wireOp",EDGE,"E1.top"),sQuery(id+"F0.wireOp",EDGE,"E1.left"),sQuery(id+"F0.wireOp",EDGE,"E1.right")])],"isStart":false})]});
            var Q7;
            Q7=makeQuery(id+"F4.boolean.opBoolean","INTERSECT",EDGE,{"derivedFrom":[makeQuery(id+"F2.opExtrude","CAP_FACE",FACE,{"disambiguationData":[OSD([sQuery(id+"F0.wireOp",EDGE,"E0.sketch_text.stroke-0"),sQuery(id+"F0.wireOp",EDGE,"E0.sketch_text.stroke-1"),sQuery(id+"F0.wireOp",EDGE,"E0.sketch_text.stroke-2"),sQuery(id+"F0.wireOp",EDGE,"E0.sketch_text.stroke-3"),sQuery(id+"F0.wireOp",EDGE,"E0.sketch_text.stroke-4"),sQuery(id+"F0.wireOp",EDGE,"E0.sketch_text.stroke-5"),sQuery(id+"F0.wireOp",EDGE,"E0.sketch_text.stroke-6"),sQuery(id+"F0.wireOp",EDGE,"E0.sketch_text.stroke-7"),sQuery(id+"F0.wireOp",EDGE,"E0.sketch_text.stroke-8"),sQuery(id+"F0.wireOp",EDGE,"E0.sketch_text.stroke-9"),sQuery(id+"F0.wireOp",EDGE,"E0.sketch_text.stroke-10"),sQuery(id+"F0.wireOp",EDGE,"E0.sketch_text.stroke-11"),sQuery(id+"F0.wireOp",EDGE,"E0.sketch_text.stroke-12"),sQuery(id+"F0.wireOp",EDGE,"E0.sketch_text.stroke-13"),sQuery(id+"F0.wireOp",EDGE,"E0.sketch_text.stroke-14"),sQuery(id+"F0.wireOp",EDGE,"E0.sketch_text.stroke-15"),sQuery(id+"F0.wireOp",EDGE,"E0.sketch_text.stroke-16"),sQuery(id+"F0.wireOp",EDGE,"E0.sketch_text.stroke-17"),sQuery(id+"F0.wireOp",EDGE,"E0.sketch_text.stroke-18"),sQuery(id+"F0.wireOp",EDGE,"E0.sketch_text.stroke-19"),sQuery(id+"F0.wireOp",EDGE,"E0.sketch_text.stroke-20"),sQuery(id+"F0.wireOp",EDGE,"E0.sketch_text.stroke-21"),sQuery(id+"F0.wireOp",EDGE,"E0.sketch_text.stroke-22"),sQuery(id+"F0.wireOp",EDGE,"E0.sketch_text.stroke-23"),sQuery(id+"F0.wireOp",EDGE,"E0.sketch_text.stroke-24"),sQuery(id+"F0.wireOp",EDGE,"E0.sketch_text.stroke-33"),sQuery(id+"F0.wireOp",EDGE,"E0.sketch_text.stroke-34"),sQuery(id+"F0.wireOp",EDGE,"E0.sketch_text.stroke-35"),sQuery(id+"F0.wireOp",EDGE,"E0.sketch_text.stroke-36"),sQuery(id+"F0.wireOp",EDGE,"E0.sketch_text.stroke-37"),sQuery(id+"F0.wireOp",EDGE,"E0.sketch_text.stroke-38"),sQuery(id+"F0.wireOp",EDGE,"E0.sketch_text.stroke-39"),sQuery(id+"F0.wireOp",EDGE,"E0.sketch_text.stroke-40"),sQuery(id+"F0.wireOp",EDGE,"E0.sketch_text.stroke-41"),sQuery(id+"F0.wireOp",EDGE,"E0.sketch_text.stroke-42"),sQuery(id+"F0.wireOp",EDGE,"E0.sketch_text.stroke-43"),sQuery(id+"F0.wireOp",EDGE,"E0.sketch_text.stroke-44"),sQuery(id+"F0.wireOp",EDGE,"E0.sketch_text.stroke-45"),sQuery(id+"F0.wireOp",EDGE,"E0.sketch_text.stroke-46"),sQuery(id+"F0.wireOp",EDGE,"E0.sketch_text.stroke-47"),sQuery(id+"F0.wireOp",EDGE,"E0.sketch_text.stroke-48"),sQuery(id+"F0.wireOp",EDGE,"E0.sketch_text.stroke-49"),sQuery(id+"F0.wireOp",EDGE,"E0.sketch_text.stroke-50"),sQuery(id+"F0.wireOp",EDGE,"E0.sketch_text.stroke-51"),sQuery(id+"F0.wireOp",EDGE,"E0.sketch_text.stroke-52"),sQuery(id+"F0.wireOp",EDGE,"E0.sketch_text.stroke-53"),sQuery(id+"F0.wireOp",EDGE,"E0.sketch_text.stroke-54"),sQuery(id+"F0.wireOp",EDGE,"E0.sketch_text.stroke-55"),sQuery(id+"F0.wireOp",EDGE,"E0.sketch_text.stroke-56"),sQuery(id+"F0.wireOp",EDGE,"E0.sketch_text.stroke-57"),sQuery(id+"F0.wireOp",EDGE,"E0.sketch_text.stroke-58"),sQuery(id+"F0.wireOp",EDGE,"E0.sketch_text.stroke-59"),sQuery(id+"F0.wireOp",EDGE,"E0.sketch_text.stroke-60"),sQuery(id+"F0.wireOp",EDGE,"E0.sketch_text.stroke-61"),sQuery(id+"F0.wireOp",EDGE,"E0.sketch_text.stroke-62"),sQuery(id+"F0.wireOp",EDGE,"E0.sketch_text.stroke-63"),sQuery(id+"F0.wireOp",EDGE,"E0.sketch_text.stroke-64"),sQuery(id+"F0.wireOp",EDGE,"E0.sketch_text.stroke-65"),sQuery(id+"F0.wireOp",EDGE,"E0.sketch_text.stroke-66"),sQuery(id+"F0.wireOp",EDGE,"E0.sketch_text.stroke-67"),sQuery(id+"F0.wireOp",EDGE,"E0.sketch_text.stroke-68"),sQuery(id+"F0.wireOp",EDGE,"E0.sketch_text.stroke-69"),sQuery(id+"F0.wireOp",EDGE,"E0.sketch_text.stroke-70"),sQuery(id+"F0.wireOp",EDGE,"E0.sketch_text.stroke-71"),sQuery(id+"F0.wireOp",EDGE,"E0.sketch_text.stroke-72"),sQuery(id+"F0.wireOp",EDGE,"E0.sketch_text.stroke-73"),sQuery(id+"F0.wireOp",EDGE,"E0.sketch_text.stroke-74"),sQuery(id+"F0.wireOp",EDGE,"E0.sketch_text.stroke-75"),sQuery(id+"F0.wireOp",EDGE,"E0.sketch_text.stroke-76"),sQuery(id+"F0.wireOp",EDGE,"E0.sketch_text.stroke-77"),sQuery(id+"F0.wireOp",EDGE,"E0.sketch_text.stroke-78"),sQuery(id+"F0.wireOp",EDGE,"E0.sketch_text.stroke-79"),sQuery(id+"F0.wireOp",EDGE,"E0.sketch_text.stroke-80"),sQuery(id+"F0.wireOp",EDGE,"E0.sketch_text.stroke-81"),sQuery(id+"F0.wireOp",EDGE,"E1.bottom"),sQuery(id+"F0.wireOp",EDGE,"E1.top"),sQuery(id+"F0.wireOp",EDGE,"E1.left"),sQuery(id+"F0.wireOp",EDGE,"E1.right")])],"isStart":false}),makeQuery(id+"F4.opExtrude","SWEPT_FACE",FACE,{"disambiguationData":[OSD([sQuery(id+"F3.wireOp",EDGE,"E7")])]})]});
            var Q8;
            Q8=makeQuery(id+"F5.opFillet","BLEND_EDGE",EDGE,{"blendedFrom":[makeQuery(id+"F4.boolean.opBoolean","COPY",EDGE,{"derivedFrom":makeQuery(id+"F4.opExtrude","SWEPT_EDGE",EDGE,{"disambiguationData":[OSD([sQuery(id+"F3.wireOp",EDGE,"E6"),sQuery(id+"F3.wireOp",EDGE,"E7")])]})}),makeQuery(id+"F2.opExtrude","CAP_FACE",FACE,{"disambiguationData":[OSD([sQuery(id+"F0.wireOp",EDGE,"E0.sketch_text.stroke-0"),sQuery(id+"F0.wireOp",EDGE,"E0.sketch_text.stroke-1"),sQuery(id+"F0.wireOp",EDGE,"E0.sketch_text.stroke-2"),sQuery(id+"F0.wireOp",EDGE,"E0.sketch_text.stroke-3"),sQuery(id+"F0.wireOp",EDGE,"E0.sketch_text.stroke-4"),sQuery(id+"F0.wireOp",EDGE,"E0.sketch_text.stroke-5"),sQuery(id+"F0.wireOp",EDGE,"E0.sketch_text.stroke-6"),sQuery(id+"F0.wireOp",EDGE,"E0.sketch_text.stroke-7"),sQuery(id+"F0.wireOp",EDGE,"E0.sketch_text.stroke-8"),sQuery(id+"F0.wireOp",EDGE,"E0.sketch_text.stroke-9"),sQuery(id+"F0.wireOp",EDGE,"E0.sketch_text.stroke-10"),sQuery(id+"F0.wireOp",EDGE,"E0.sketch_text.stroke-11"),sQuery(id+"F0.wireOp",EDGE,"E0.sketch_text.stroke-12"),sQuery(id+"F0.wireOp",EDGE,"E0.sketch_text.stroke-13"),sQuery(id+"F0.wireOp",EDGE,"E0.sketch_text.stroke-14"),sQuery(id+"F0.wireOp",EDGE,"E0.sketch_text.stroke-15"),sQuery(id+"F0.wireOp",EDGE,"E0.sketch_text.stroke-16"),sQuery(id+"F0.wireOp",EDGE,"E0.sketch_text.stroke-17"),sQuery(id+"F0.wireOp",EDGE,"E0.sketch_text.stroke-18"),sQuery(id+"F0.wireOp",EDGE,"E0.sketch_text.stroke-19"),sQuery(id+"F0.wireOp",EDGE,"E0.sketch_text.stroke-20"),sQuery(id+"F0.wireOp",EDGE,"E0.sketch_text.stroke-21"),sQuery(id+"F0.wireOp",EDGE,"E0.sketch_text.stroke-22"),sQuery(id+"F0.wireOp",EDGE,"E0.sketch_text.stroke-23"),sQuery(id+"F0.wireOp",EDGE,"E0.sketch_text.stroke-24"),sQuery(id+"F0.wireOp",EDGE,"E0.sketch_text.stroke-33"),sQuery(id+"F0.wireOp",EDGE,"E0.sketch_text.stroke-34"),sQuery(id+"F0.wireOp",EDGE,"E0.sketch_text.stroke-35"),sQuery(id+"F0.wireOp",EDGE,"E0.sketch_text.stroke-36"),sQuery(id+"F0.wireOp",EDGE,"E0.sketch_text.stroke-37"),sQuery(id+"F0.wireOp",EDGE,"E0.sketch_text.stroke-38"),sQuery(id+"F0.wireOp",EDGE,"E0.sketch_text.stroke-39"),sQuery(id+"F0.wireOp",EDGE,"E0.sketch_text.stroke-40"),sQuery(id+"F0.wireOp",EDGE,"E0.sketch_text.stroke-41"),sQuery(id+"F0.wireOp",EDGE,"E0.sketch_text.stroke-42"),sQuery(id+"F0.wireOp",EDGE,"E0.sketch_text.stroke-43"),sQuery(id+"F0.wireOp",EDGE,"E0.sketch_text.stroke-44"),sQuery(id+"F0.wireOp",EDGE,"E0.sketch_text.stroke-45"),sQuery(id+"F0.wireOp",EDGE,"E0.sketch_text.stroke-46"),sQuery(id+"F0.wireOp",EDGE,"E0.sketch_text.stroke-47"),sQuery(id+"F0.wireOp",EDGE,"E0.sketch_text.stroke-48"),sQuery(id+"F0.wireOp",EDGE,"E0.sketch_text.stroke-49"),sQuery(id+"F0.wireOp",EDGE,"E0.sketch_text.stroke-50"),sQuery(id+"F0.wireOp",EDGE,"E0.sketch_text.stroke-51"),sQuery(id+"F0.wireOp",EDGE,"E0.sketch_text.stroke-52"),sQuery(id+"F0.wireOp",EDGE,"E0.sketch_text.stroke-53"),sQuery(id+"F0.wireOp",EDGE,"E0.sketch_text.stroke-54"),sQuery(id+"F0.wireOp",EDGE,"E0.sketch_text.stroke-55"),sQuery(id+"F0.wireOp",EDGE,"E0.sketch_text.stroke-56"),sQuery(id+"F0.wireOp",EDGE,"E0.sketch_text.stroke-57"),sQuery(id+"F0.wireOp",EDGE,"E0.sketch_text.stroke-58"),sQuery(id+"F0.wireOp",EDGE,"E0.sketch_text.stroke-59"),sQuery(id+"F0.wireOp",EDGE,"E0.sketch_text.stroke-60"),sQuery(id+"F0.wireOp",EDGE,"E0.sketch_text.stroke-61"),sQuery(id+"F0.wireOp",EDGE,"E0.sketch_text.stroke-62"),sQuery(id+"F0.wireOp",EDGE,"E0.sketch_text.stroke-63"),sQuery(id+"F0.wireOp",EDGE,"E0.sketch_text.stroke-64"),sQuery(id+"F0.wireOp",EDGE,"E0.sketch_text.stroke-65"),sQuery(id+"F0.wireOp",EDGE,"E0.sketch_text.stroke-66"),sQuery(id+"F0.wireOp",EDGE,"E0.sketch_text.stroke-67"),sQuery(id+"F0.wireOp",EDGE,"E0.sketch_text.stroke-68"),sQuery(id+"F0.wireOp",EDGE,"E0.sketch_text.stroke-69"),sQuery(id+"F0.wireOp",EDGE,"E0.sketch_text.stroke-70"),sQuery(id+"F0.wireOp",EDGE,"E0.sketch_text.stroke-71"),sQuery(id+"F0.wireOp",EDGE,"E0.sketch_text.stroke-72"),sQuery(id+"F0.wireOp",EDGE,"E0.sketch_text.stroke-73"),sQuery(id+"F0.wireOp",EDGE,"E0.sketch_text.stroke-74"),sQuery(id+"F0.wireOp",EDGE,"E0.sketch_text.stroke-75"),sQuery(id+"F0.wireOp",EDGE,"E0.sketch_text.stroke-76"),sQuery(id+"F0.wireOp",EDGE,"E0.sketch_text.stroke-77"),sQuery(id+"F0.wireOp",EDGE,"E0.sketch_text.stroke-78"),sQuery(id+"F0.wireOp",EDGE,"E0.sketch_text.stroke-79"),sQuery(id+"F0.wireOp",EDGE,"E0.sketch_text.stroke-80"),sQuery(id+"F0.wireOp",EDGE,"E0.sketch_text.stroke-81"),sQuery(id+"F0.wireOp",EDGE,"E1.bottom"),sQuery(id+"F0.wireOp",EDGE,"E1.top"),sQuery(id+"F0.wireOp",EDGE,"E1.left"),sQuery(id+"F0.wireOp",EDGE,"E1.right")])],"isStart":false})],"blendedInto":[makeQuery(id+"F2.opExtrude","CAP_FACE",FACE,{"disambiguationData":[OSD([sQuery(id+"F0.wireOp",EDGE,"E0.sketch_text.stroke-0"),sQuery(id+"F0.wireOp",EDGE,"E0.sketch_text.stroke-1"),sQuery(id+"F0.wireOp",EDGE,"E0.sketch_text.stroke-2"),sQuery(id+"F0.wireOp",EDGE,"E0.sketch_text.stroke-3"),sQuery(id+"F0.wireOp",EDGE,"E0.sketch_text.stroke-4"),sQuery(id+"F0.wireOp",EDGE,"E0.sketch_text.stroke-5"),sQuery(id+"F0.wireOp",EDGE,"E0.sketch_text.stroke-6"),sQuery(id+"F0.wireOp",EDGE,"E0.sketch_text.stroke-7"),sQuery(id+"F0.wireOp",EDGE,"E0.sketch_text.stroke-8"),sQuery(id+"F0.wireOp",EDGE,"E0.sketch_text.stroke-9"),sQuery(id+"F0.wireOp",EDGE,"E0.sketch_text.stroke-10"),sQuery(id+"F0.wireOp",EDGE,"E0.sketch_text.stroke-11"),sQuery(id+"F0.wireOp",EDGE,"E0.sketch_text.stroke-12"),sQuery(id+"F0.wireOp",EDGE,"E0.sketch_text.stroke-13"),sQuery(id+"F0.wireOp",EDGE,"E0.sketch_text.stroke-14"),sQuery(id+"F0.wireOp",EDGE,"E0.sketch_text.stroke-15"),sQuery(id+"F0.wireOp",EDGE,"E0.sketch_text.stroke-16"),sQuery(id+"F0.wireOp",EDGE,"E0.sketch_text.stroke-17"),sQuery(id+"F0.wireOp",EDGE,"E0.sketch_text.stroke-18"),sQuery(id+"F0.wireOp",EDGE,"E0.sketch_text.stroke-19"),sQuery(id+"F0.wireOp",EDGE,"E0.sketch_text.stroke-20"),sQuery(id+"F0.wireOp",EDGE,"E0.sketch_text.stroke-21"),sQuery(id+"F0.wireOp",EDGE,"E0.sketch_text.stroke-22"),sQuery(id+"F0.wireOp",EDGE,"E0.sketch_text.stroke-23"),sQuery(id+"F0.wireOp",EDGE,"E0.sketch_text.stroke-24"),sQuery(id+"F0.wireOp",EDGE,"E0.sketch_text.stroke-33"),sQuery(id+"F0.wireOp",EDGE,"E0.sketch_text.stroke-34"),sQuery(id+"F0.wireOp",EDGE,"E0.sketch_text.stroke-35"),sQuery(id+"F0.wireOp",EDGE,"E0.sketch_text.stroke-36"),sQuery(id+"F0.wireOp",EDGE,"E0.sketch_text.stroke-37"),sQuery(id+"F0.wireOp",EDGE,"E0.sketch_text.stroke-38"),sQuery(id+"F0.wireOp",EDGE,"E0.sketch_text.stroke-39"),sQuery(id+"F0.wireOp",EDGE,"E0.sketch_text.stroke-40"),sQuery(id+"F0.wireOp",EDGE,"E0.sketch_text.stroke-41"),sQuery(id+"F0.wireOp",EDGE,"E0.sketch_text.stroke-42"),sQuery(id+"F0.wireOp",EDGE,"E0.sketch_text.stroke-43"),sQuery(id+"F0.wireOp",EDGE,"E0.sketch_text.stroke-44"),sQuery(id+"F0.wireOp",EDGE,"E0.sketch_text.stroke-45"),sQuery(id+"F0.wireOp",EDGE,"E0.sketch_text.stroke-46"),sQuery(id+"F0.wireOp",EDGE,"E0.sketch_text.stroke-47"),sQuery(id+"F0.wireOp",EDGE,"E0.sketch_text.stroke-48"),sQuery(id+"F0.wireOp",EDGE,"E0.sketch_text.stroke-49"),sQuery(id+"F0.wireOp",EDGE,"E0.sketch_text.stroke-50"),sQuery(id+"F0.wireOp",EDGE,"E0.sketch_text.stroke-51"),sQuery(id+"F0.wireOp",EDGE,"E0.sketch_text.stroke-52"),sQuery(id+"F0.wireOp",EDGE,"E0.sketch_text.stroke-53"),sQuery(id+"F0.wireOp",EDGE,"E0.sketch_text.stroke-54"),sQuery(id+"F0.wireOp",EDGE,"E0.sketch_text.stroke-55"),sQuery(id+"F0.wireOp",EDGE,"E0.sketch_text.stroke-56"),sQuery(id+"F0.wireOp",EDGE,"E0.sketch_text.stroke-57"),sQuery(id+"F0.wireOp",EDGE,"E0.sketch_text.stroke-58"),sQuery(id+"F0.wireOp",EDGE,"E0.sketch_text.stroke-59"),sQuery(id+"F0.wireOp",EDGE,"E0.sketch_text.stroke-60"),sQuery(id+"F0.wireOp",EDGE,"E0.sketch_text.stroke-61"),sQuery(id+"F0.wireOp",EDGE,"E0.sketch_text.stroke-62"),sQuery(id+"F0.wireOp",EDGE,"E0.sketch_text.stroke-63"),sQuery(id+"F0.wireOp",EDGE,"E0.sketch_text.stroke-64"),sQuery(id+"F0.wireOp",EDGE,"E0.sketch_text.stroke-65"),sQuery(id+"F0.wireOp",EDGE,"E0.sketch_text.stroke-66"),sQuery(id+"F0.wireOp",EDGE,"E0.sketch_text.stroke-67"),sQuery(id+"F0.wireOp",EDGE,"E0.sketch_text.stroke-68"),sQuery(id+"F0.wireOp",EDGE,"E0.sketch_text.stroke-69"),sQuery(id+"F0.wireOp",EDGE,"E0.sketch_text.stroke-70"),sQuery(id+"F0.wireOp",EDGE,"E0.sketch_text.stroke-71"),sQuery(id+"F0.wireOp",EDGE,"E0.sketch_text.stroke-72"),sQuery(id+"F0.wireOp",EDGE,"E0.sketch_text.stroke-73"),sQuery(id+"F0.wireOp",EDGE,"E0.sketch_text.stroke-74"),sQuery(id+"F0.wireOp",EDGE,"E0.sketch_text.stroke-75"),sQuery(id+"F0.wireOp",EDGE,"E0.sketch_text.stroke-76"),sQuery(id+"F0.wireOp",EDGE,"E0.sketch_text.stroke-77"),sQuery(id+"F0.wireOp",EDGE,"E0.sketch_text.stroke-78"),sQuery(id+"F0.wireOp",EDGE,"E0.sketch_text.stroke-79"),sQuery(id+"F0.wireOp",EDGE,"E0.sketch_text.stroke-80"),sQuery(id+"F0.wireOp",EDGE,"E0.sketch_text.stroke-81"),sQuery(id+"F0.wireOp",EDGE,"E1.bottom"),sQuery(id+"F0.wireOp",EDGE,"E1.top"),sQuery(id+"F0.wireOp",EDGE,"E1.left"),sQuery(id+"F0.wireOp",EDGE,"E1.right")])],"isStart":false})]});
            var Q9;
            Q9=makeQuery(id+"F4.boolean.opBoolean","INTERSECT",EDGE,{"derivedFrom":[makeQuery(id+"F2.opExtrude","CAP_FACE",FACE,{"disambiguationData":[OSD([sQuery(id+"F0.wireOp",EDGE,"E0.sketch_text.stroke-0"),sQuery(id+"F0.wireOp",EDGE,"E0.sketch_text.stroke-1"),sQuery(id+"F0.wireOp",EDGE,"E0.sketch_text.stroke-2"),sQuery(id+"F0.wireOp",EDGE,"E0.sketch_text.stroke-3"),sQuery(id+"F0.wireOp",EDGE,"E0.sketch_text.stroke-4"),sQuery(id+"F0.wireOp",EDGE,"E0.sketch_text.stroke-5"),sQuery(id+"F0.wireOp",EDGE,"E0.sketch_text.stroke-6"),sQuery(id+"F0.wireOp",EDGE,"E0.sketch_text.stroke-7"),sQuery(id+"F0.wireOp",EDGE,"E0.sketch_text.stroke-8"),sQuery(id+"F0.wireOp",EDGE,"E0.sketch_text.stroke-9"),sQuery(id+"F0.wireOp",EDGE,"E0.sketch_text.stroke-10"),sQuery(id+"F0.wireOp",EDGE,"E0.sketch_text.stroke-11"),sQuery(id+"F0.wireOp",EDGE,"E0.sketch_text.stroke-12"),sQuery(id+"F0.wireOp",EDGE,"E0.sketch_text.stroke-13"),sQuery(id+"F0.wireOp",EDGE,"E0.sketch_text.stroke-14"),sQuery(id+"F0.wireOp",EDGE,"E0.sketch_text.stroke-15"),sQuery(id+"F0.wireOp",EDGE,"E0.sketch_text.stroke-16"),sQuery(id+"F0.wireOp",EDGE,"E0.sketch_text.stroke-17"),sQuery(id+"F0.wireOp",EDGE,"E0.sketch_text.stroke-18"),sQuery(id+"F0.wireOp",EDGE,"E0.sketch_text.stroke-19"),sQuery(id+"F0.wireOp",EDGE,"E0.sketch_text.stroke-20"),sQuery(id+"F0.wireOp",EDGE,"E0.sketch_text.stroke-21"),sQuery(id+"F0.wireOp",EDGE,"E0.sketch_text.stroke-22"),sQuery(id+"F0.wireOp",EDGE,"E0.sketch_text.stroke-23"),sQuery(id+"F0.wireOp",EDGE,"E0.sketch_text.stroke-24"),sQuery(id+"F0.wireOp",EDGE,"E0.sketch_text.stroke-33"),sQuery(id+"F0.wireOp",EDGE,"E0.sketch_text.stroke-34"),sQuery(id+"F0.wireOp",EDGE,"E0.sketch_text.stroke-35"),sQuery(id+"F0.wireOp",EDGE,"E0.sketch_text.stroke-36"),sQuery(id+"F0.wireOp",EDGE,"E0.sketch_text.stroke-37"),sQuery(id+"F0.wireOp",EDGE,"E0.sketch_text.stroke-38"),sQuery(id+"F0.wireOp",EDGE,"E0.sketch_text.stroke-39"),sQuery(id+"F0.wireOp",EDGE,"E0.sketch_text.stroke-40"),sQuery(id+"F0.wireOp",EDGE,"E0.sketch_text.stroke-41"),sQuery(id+"F0.wireOp",EDGE,"E0.sketch_text.stroke-42"),sQuery(id+"F0.wireOp",EDGE,"E0.sketch_text.stroke-43"),sQuery(id+"F0.wireOp",EDGE,"E0.sketch_text.stroke-44"),sQuery(id+"F0.wireOp",EDGE,"E0.sketch_text.stroke-45"),sQuery(id+"F0.wireOp",EDGE,"E0.sketch_text.stroke-46"),sQuery(id+"F0.wireOp",EDGE,"E0.sketch_text.stroke-47"),sQuery(id+"F0.wireOp",EDGE,"E0.sketch_text.stroke-48"),sQuery(id+"F0.wireOp",EDGE,"E0.sketch_text.stroke-49"),sQuery(id+"F0.wireOp",EDGE,"E0.sketch_text.stroke-50"),sQuery(id+"F0.wireOp",EDGE,"E0.sketch_text.stroke-51"),sQuery(id+"F0.wireOp",EDGE,"E0.sketch_text.stroke-52"),sQuery(id+"F0.wireOp",EDGE,"E0.sketch_text.stroke-53"),sQuery(id+"F0.wireOp",EDGE,"E0.sketch_text.stroke-54"),sQuery(id+"F0.wireOp",EDGE,"E0.sketch_text.stroke-55"),sQuery(id+"F0.wireOp",EDGE,"E0.sketch_text.stroke-56"),sQuery(id+"F0.wireOp",EDGE,"E0.sketch_text.stroke-57"),sQuery(id+"F0.wireOp",EDGE,"E0.sketch_text.stroke-58"),sQuery(id+"F0.wireOp",EDGE,"E0.sketch_text.stroke-59"),sQuery(id+"F0.wireOp",EDGE,"E0.sketch_text.stroke-60"),sQuery(id+"F0.wireOp",EDGE,"E0.sketch_text.stroke-61"),sQuery(id+"F0.wireOp",EDGE,"E0.sketch_text.stroke-62"),sQuery(id+"F0.wireOp",EDGE,"E0.sketch_text.stroke-63"),sQuery(id+"F0.wireOp",EDGE,"E0.sketch_text.stroke-64"),sQuery(id+"F0.wireOp",EDGE,"E0.sketch_text.stroke-65"),sQuery(id+"F0.wireOp",EDGE,"E0.sketch_text.stroke-66"),sQuery(id+"F0.wireOp",EDGE,"E0.sketch_text.stroke-67"),sQuery(id+"F0.wireOp",EDGE,"E0.sketch_text.stroke-68"),sQuery(id+"F0.wireOp",EDGE,"E0.sketch_text.stroke-69"),sQuery(id+"F0.wireOp",EDGE,"E0.sketch_text.stroke-70"),sQuery(id+"F0.wireOp",EDGE,"E0.sketch_text.stroke-71"),sQuery(id+"F0.wireOp",EDGE,"E0.sketch_text.stroke-72"),sQuery(id+"F0.wireOp",EDGE,"E0.sketch_text.stroke-73"),sQuery(id+"F0.wireOp",EDGE,"E0.sketch_text.stroke-74"),sQuery(id+"F0.wireOp",EDGE,"E0.sketch_text.stroke-75"),sQuery(id+"F0.wireOp",EDGE,"E0.sketch_text.stroke-76"),sQuery(id+"F0.wireOp",EDGE,"E0.sketch_text.stroke-77"),sQuery(id+"F0.wireOp",EDGE,"E0.sketch_text.stroke-78"),sQuery(id+"F0.wireOp",EDGE,"E0.sketch_text.stroke-79"),sQuery(id+"F0.wireOp",EDGE,"E0.sketch_text.stroke-80"),sQuery(id+"F0.wireOp",EDGE,"E0.sketch_text.stroke-81"),sQuery(id+"F0.wireOp",EDGE,"E1.bottom"),sQuery(id+"F0.wireOp",EDGE,"E1.top"),sQuery(id+"F0.wireOp",EDGE,"E1.left"),sQuery(id+"F0.wireOp",EDGE,"E1.right")])],"isStart":false}),makeQuery(id+"F4.opExtrude","SWEPT_FACE",FACE,{"disambiguationData":[OSD([sQuery(id+"F3.wireOp",EDGE,"E6")])]})]});
            var Q10;
            Q10=makeQuery(id+"F5.opFillet","BLEND_EDGE",EDGE,{"blendedFrom":[makeQuery(id+"F4.boolean.opBoolean","COPY",EDGE,{"derivedFrom":makeQuery(id+"F4.opExtrude","SWEPT_EDGE",EDGE,{"disambiguationData":[OSD([sQuery(id+"F3.wireOp",EDGE,"E5.0"),sQuery(id+"F3.wireOp",EDGE,"E6")])]})}),makeQuery(id+"F2.opExtrude","CAP_FACE",FACE,{"disambiguationData":[OSD([sQuery(id+"F0.wireOp",EDGE,"E0.sketch_text.stroke-0"),sQuery(id+"F0.wireOp",EDGE,"E0.sketch_text.stroke-1"),sQuery(id+"F0.wireOp",EDGE,"E0.sketch_text.stroke-2"),sQuery(id+"F0.wireOp",EDGE,"E0.sketch_text.stroke-3"),sQuery(id+"F0.wireOp",EDGE,"E0.sketch_text.stroke-4"),sQuery(id+"F0.wireOp",EDGE,"E0.sketch_text.stroke-5"),sQuery(id+"F0.wireOp",EDGE,"E0.sketch_text.stroke-6"),sQuery(id+"F0.wireOp",EDGE,"E0.sketch_text.stroke-7"),sQuery(id+"F0.wireOp",EDGE,"E0.sketch_text.stroke-8"),sQuery(id+"F0.wireOp",EDGE,"E0.sketch_text.stroke-9"),sQuery(id+"F0.wireOp",EDGE,"E0.sketch_text.stroke-10"),sQuery(id+"F0.wireOp",EDGE,"E0.sketch_text.stroke-11"),sQuery(id+"F0.wireOp",EDGE,"E0.sketch_text.stroke-12"),sQuery(id+"F0.wireOp",EDGE,"E0.sketch_text.stroke-13"),sQuery(id+"F0.wireOp",EDGE,"E0.sketch_text.stroke-14"),sQuery(id+"F0.wireOp",EDGE,"E0.sketch_text.stroke-15"),sQuery(id+"F0.wireOp",EDGE,"E0.sketch_text.stroke-16"),sQuery(id+"F0.wireOp",EDGE,"E0.sketch_text.stroke-17"),sQuery(id+"F0.wireOp",EDGE,"E0.sketch_text.stroke-18"),sQuery(id+"F0.wireOp",EDGE,"E0.sketch_text.stroke-19"),sQuery(id+"F0.wireOp",EDGE,"E0.sketch_text.stroke-20"),sQuery(id+"F0.wireOp",EDGE,"E0.sketch_text.stroke-21"),sQuery(id+"F0.wireOp",EDGE,"E0.sketch_text.stroke-22"),sQuery(id+"F0.wireOp",EDGE,"E0.sketch_text.stroke-23"),sQuery(id+"F0.wireOp",EDGE,"E0.sketch_text.stroke-24"),sQuery(id+"F0.wireOp",EDGE,"E0.sketch_text.stroke-33"),sQuery(id+"F0.wireOp",EDGE,"E0.sketch_text.stroke-34"),sQuery(id+"F0.wireOp",EDGE,"E0.sketch_text.stroke-35"),sQuery(id+"F0.wireOp",EDGE,"E0.sketch_text.stroke-36"),sQuery(id+"F0.wireOp",EDGE,"E0.sketch_text.stroke-37"),sQuery(id+"F0.wireOp",EDGE,"E0.sketch_text.stroke-38"),sQuery(id+"F0.wireOp",EDGE,"E0.sketch_text.stroke-39"),sQuery(id+"F0.wireOp",EDGE,"E0.sketch_text.stroke-40"),sQuery(id+"F0.wireOp",EDGE,"E0.sketch_text.stroke-41"),sQuery(id+"F0.wireOp",EDGE,"E0.sketch_text.stroke-42"),sQuery(id+"F0.wireOp",EDGE,"E0.sketch_text.stroke-43"),sQuery(id+"F0.wireOp",EDGE,"E0.sketch_text.stroke-44"),sQuery(id+"F0.wireOp",EDGE,"E0.sketch_text.stroke-45"),sQuery(id+"F0.wireOp",EDGE,"E0.sketch_text.stroke-46"),sQuery(id+"F0.wireOp",EDGE,"E0.sketch_text.stroke-47"),sQuery(id+"F0.wireOp",EDGE,"E0.sketch_text.stroke-48"),sQuery(id+"F0.wireOp",EDGE,"E0.sketch_text.stroke-49"),sQuery(id+"F0.wireOp",EDGE,"E0.sketch_text.stroke-50"),sQuery(id+"F0.wireOp",EDGE,"E0.sketch_text.stroke-51"),sQuery(id+"F0.wireOp",EDGE,"E0.sketch_text.stroke-52"),sQuery(id+"F0.wireOp",EDGE,"E0.sketch_text.stroke-53"),sQuery(id+"F0.wireOp",EDGE,"E0.sketch_text.stroke-54"),sQuery(id+"F0.wireOp",EDGE,"E0.sketch_text.stroke-55"),sQuery(id+"F0.wireOp",EDGE,"E0.sketch_text.stroke-56"),sQuery(id+"F0.wireOp",EDGE,"E0.sketch_text.stroke-57"),sQuery(id+"F0.wireOp",EDGE,"E0.sketch_text.stroke-58"),sQuery(id+"F0.wireOp",EDGE,"E0.sketch_text.stroke-59"),sQuery(id+"F0.wireOp",EDGE,"E0.sketch_text.stroke-60"),sQuery(id+"F0.wireOp",EDGE,"E0.sketch_text.stroke-61"),sQuery(id+"F0.wireOp",EDGE,"E0.sketch_text.stroke-62"),sQuery(id+"F0.wireOp",EDGE,"E0.sketch_text.stroke-63"),sQuery(id+"F0.wireOp",EDGE,"E0.sketch_text.stroke-64"),sQuery(id+"F0.wireOp",EDGE,"E0.sketch_text.stroke-65"),sQuery(id+"F0.wireOp",EDGE,"E0.sketch_text.stroke-66"),sQuery(id+"F0.wireOp",EDGE,"E0.sketch_text.stroke-67"),sQuery(id+"F0.wireOp",EDGE,"E0.sketch_text.stroke-68"),sQuery(id+"F0.wireOp",EDGE,"E0.sketch_text.stroke-69"),sQuery(id+"F0.wireOp",EDGE,"E0.sketch_text.stroke-70"),sQuery(id+"F0.wireOp",EDGE,"E0.sketch_text.stroke-71"),sQuery(id+"F0.wireOp",EDGE,"E0.sketch_text.stroke-72"),sQuery(id+"F0.wireOp",EDGE,"E0.sketch_text.stroke-73"),sQuery(id+"F0.wireOp",EDGE,"E0.sketch_text.stroke-74"),sQuery(id+"F0.wireOp",EDGE,"E0.sketch_text.stroke-75"),sQuery(id+"F0.wireOp",EDGE,"E0.sketch_text.stroke-76"),sQuery(id+"F0.wireOp",EDGE,"E0.sketch_text.stroke-77"),sQuery(id+"F0.wireOp",EDGE,"E0.sketch_text.stroke-78"),sQuery(id+"F0.wireOp",EDGE,"E0.sketch_text.stroke-79"),sQuery(id+"F0.wireOp",EDGE,"E0.sketch_text.stroke-80"),sQuery(id+"F0.wireOp",EDGE,"E0.sketch_text.stroke-81"),sQuery(id+"F0.wireOp",EDGE,"E1.bottom"),sQuery(id+"F0.wireOp",EDGE,"E1.top"),sQuery(id+"F0.wireOp",EDGE,"E1.left"),sQuery(id+"F0.wireOp",EDGE,"E1.right")])],"isStart":false})],"blendedInto":[makeQuery(id+"F2.opExtrude","CAP_FACE",FACE,{"disambiguationData":[OSD([sQuery(id+"F0.wireOp",EDGE,"E0.sketch_text.stroke-0"),sQuery(id+"F0.wireOp",EDGE,"E0.sketch_text.stroke-1"),sQuery(id+"F0.wireOp",EDGE,"E0.sketch_text.stroke-2"),sQuery(id+"F0.wireOp",EDGE,"E0.sketch_text.stroke-3"),sQuery(id+"F0.wireOp",EDGE,"E0.sketch_text.stroke-4"),sQuery(id+"F0.wireOp",EDGE,"E0.sketch_text.stroke-5"),sQuery(id+"F0.wireOp",EDGE,"E0.sketch_text.stroke-6"),sQuery(id+"F0.wireOp",EDGE,"E0.sketch_text.stroke-7"),sQuery(id+"F0.wireOp",EDGE,"E0.sketch_text.stroke-8"),sQuery(id+"F0.wireOp",EDGE,"E0.sketch_text.stroke-9"),sQuery(id+"F0.wireOp",EDGE,"E0.sketch_text.stroke-10"),sQuery(id+"F0.wireOp",EDGE,"E0.sketch_text.stroke-11"),sQuery(id+"F0.wireOp",EDGE,"E0.sketch_text.stroke-12"),sQuery(id+"F0.wireOp",EDGE,"E0.sketch_text.stroke-13"),sQuery(id+"F0.wireOp",EDGE,"E0.sketch_text.stroke-14"),sQuery(id+"F0.wireOp",EDGE,"E0.sketch_text.stroke-15"),sQuery(id+"F0.wireOp",EDGE,"E0.sketch_text.stroke-16"),sQuery(id+"F0.wireOp",EDGE,"E0.sketch_text.stroke-17"),sQuery(id+"F0.wireOp",EDGE,"E0.sketch_text.stroke-18"),sQuery(id+"F0.wireOp",EDGE,"E0.sketch_text.stroke-19"),sQuery(id+"F0.wireOp",EDGE,"E0.sketch_text.stroke-20"),sQuery(id+"F0.wireOp",EDGE,"E0.sketch_text.stroke-21"),sQuery(id+"F0.wireOp",EDGE,"E0.sketch_text.stroke-22"),sQuery(id+"F0.wireOp",EDGE,"E0.sketch_text.stroke-23"),sQuery(id+"F0.wireOp",EDGE,"E0.sketch_text.stroke-24"),sQuery(id+"F0.wireOp",EDGE,"E0.sketch_text.stroke-33"),sQuery(id+"F0.wireOp",EDGE,"E0.sketch_text.stroke-34"),sQuery(id+"F0.wireOp",EDGE,"E0.sketch_text.stroke-35"),sQuery(id+"F0.wireOp",EDGE,"E0.sketch_text.stroke-36"),sQuery(id+"F0.wireOp",EDGE,"E0.sketch_text.stroke-37"),sQuery(id+"F0.wireOp",EDGE,"E0.sketch_text.stroke-38"),sQuery(id+"F0.wireOp",EDGE,"E0.sketch_text.stroke-39"),sQuery(id+"F0.wireOp",EDGE,"E0.sketch_text.stroke-40"),sQuery(id+"F0.wireOp",EDGE,"E0.sketch_text.stroke-41"),sQuery(id+"F0.wireOp",EDGE,"E0.sketch_text.stroke-42"),sQuery(id+"F0.wireOp",EDGE,"E0.sketch_text.stroke-43"),sQuery(id+"F0.wireOp",EDGE,"E0.sketch_text.stroke-44"),sQuery(id+"F0.wireOp",EDGE,"E0.sketch_text.stroke-45"),sQuery(id+"F0.wireOp",EDGE,"E0.sketch_text.stroke-46"),sQuery(id+"F0.wireOp",EDGE,"E0.sketch_text.stroke-47"),sQuery(id+"F0.wireOp",EDGE,"E0.sketch_text.stroke-48"),sQuery(id+"F0.wireOp",EDGE,"E0.sketch_text.stroke-49"),sQuery(id+"F0.wireOp",EDGE,"E0.sketch_text.stroke-50"),sQuery(id+"F0.wireOp",EDGE,"E0.sketch_text.stroke-51"),sQuery(id+"F0.wireOp",EDGE,"E0.sketch_text.stroke-52"),sQuery(id+"F0.wireOp",EDGE,"E0.sketch_text.stroke-53"),sQuery(id+"F0.wireOp",EDGE,"E0.sketch_text.stroke-54"),sQuery(id+"F0.wireOp",EDGE,"E0.sketch_text.stroke-55"),sQuery(id+"F0.wireOp",EDGE,"E0.sketch_text.stroke-56"),sQuery(id+"F0.wireOp",EDGE,"E0.sketch_text.stroke-57"),sQuery(id+"F0.wireOp",EDGE,"E0.sketch_text.stroke-58"),sQuery(id+"F0.wireOp",EDGE,"E0.sketch_text.stroke-59"),sQuery(id+"F0.wireOp",EDGE,"E0.sketch_text.stroke-60"),sQuery(id+"F0.wireOp",EDGE,"E0.sketch_text.stroke-61"),sQuery(id+"F0.wireOp",EDGE,"E0.sketch_text.stroke-62"),sQuery(id+"F0.wireOp",EDGE,"E0.sketch_text.stroke-63"),sQuery(id+"F0.wireOp",EDGE,"E0.sketch_text.stroke-64"),sQuery(id+"F0.wireOp",EDGE,"E0.sketch_text.stroke-65"),sQuery(id+"F0.wireOp",EDGE,"E0.sketch_text.stroke-66"),sQuery(id+"F0.wireOp",EDGE,"E0.sketch_text.stroke-67"),sQuery(id+"F0.wireOp",EDGE,"E0.sketch_text.stroke-68"),sQuery(id+"F0.wireOp",EDGE,"E0.sketch_text.stroke-69"),sQuery(id+"F0.wireOp",EDGE,"E0.sketch_text.stroke-70"),sQuery(id+"F0.wireOp",EDGE,"E0.sketch_text.stroke-71"),sQuery(id+"F0.wireOp",EDGE,"E0.sketch_text.stroke-72"),sQuery(id+"F0.wireOp",EDGE,"E0.sketch_text.stroke-73"),sQuery(id+"F0.wireOp",EDGE,"E0.sketch_text.stroke-74"),sQuery(id+"F0.wireOp",EDGE,"E0.sketch_text.stroke-75"),sQuery(id+"F0.wireOp",EDGE,"E0.sketch_text.stroke-76"),sQuery(id+"F0.wireOp",EDGE,"E0.sketch_text.stroke-77"),sQuery(id+"F0.wireOp",EDGE,"E0.sketch_text.stroke-78"),sQuery(id+"F0.wireOp",EDGE,"E0.sketch_text.stroke-79"),sQuery(id+"F0.wireOp",EDGE,"E0.sketch_text.stroke-80"),sQuery(id+"F0.wireOp",EDGE,"E0.sketch_text.stroke-81"),sQuery(id+"F0.wireOp",EDGE,"E1.bottom"),sQuery(id+"F0.wireOp",EDGE,"E1.top"),sQuery(id+"F0.wireOp",EDGE,"E1.left"),sQuery(id+"F0.wireOp",EDGE,"E1.right")])],"isStart":false})]});
            fillet(context, id + "F7", {"entities" : qUnion([Q0, Q1, Q2, Q3, Q4, Q5, Q6, Q7, Q8, Q9, Q10]), "tangentPropagation" : true, "radius" : 1.8 * mm, "defaultsChanged" : true, "vertexSettings" : [], "allowEdgeOverflow" : false});
        }
    });
